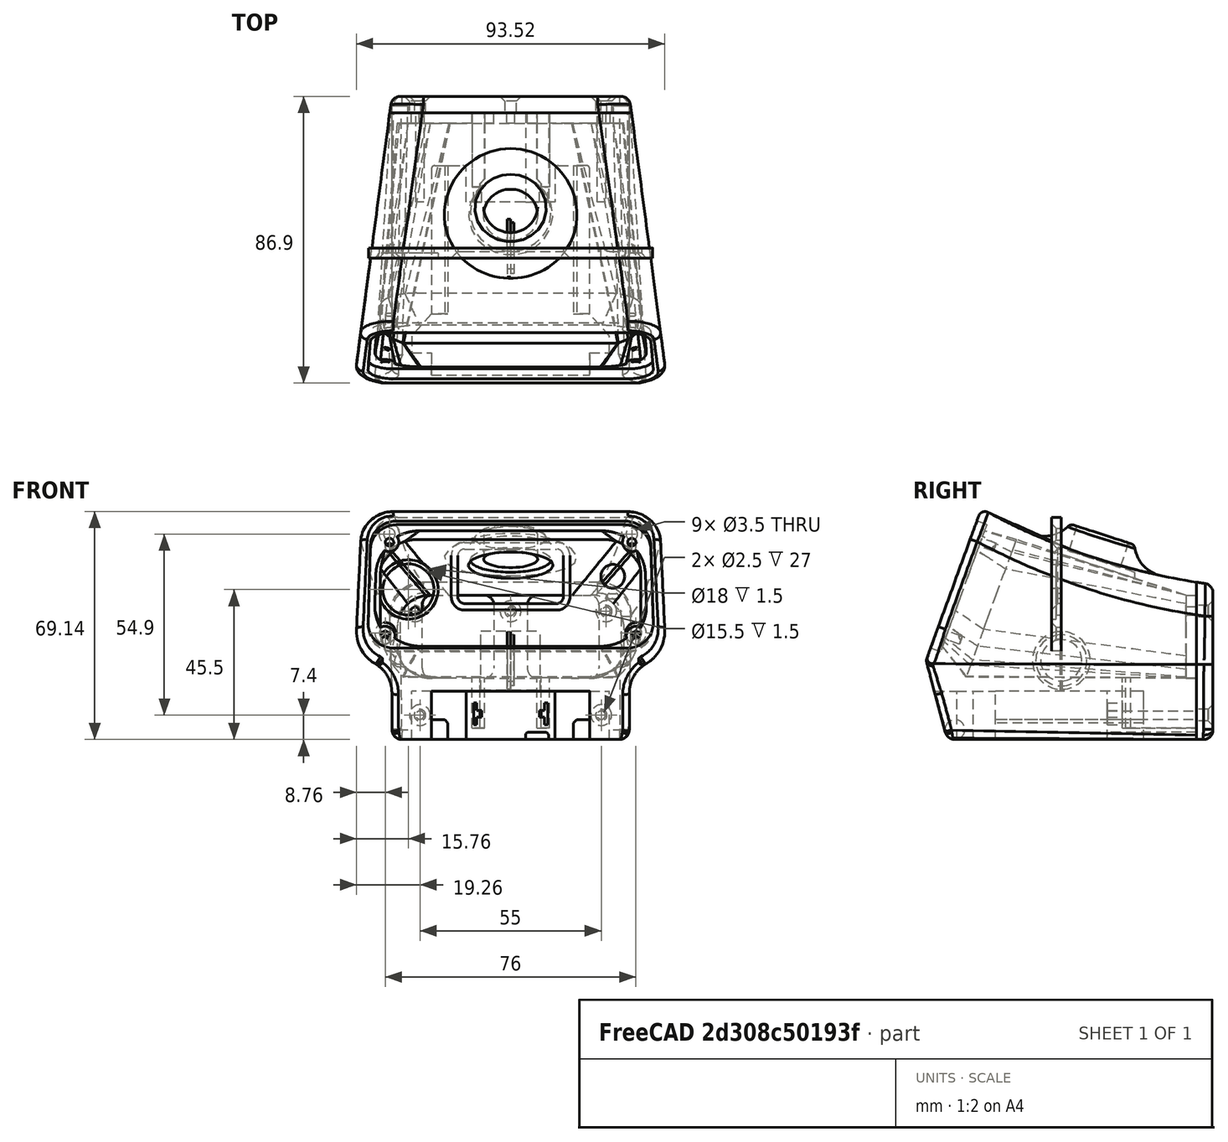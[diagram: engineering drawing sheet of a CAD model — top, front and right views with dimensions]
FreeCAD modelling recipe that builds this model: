
FCSTD DOCUMENT  (FreeCAD 2021.504R24301 +3511 (Git))
Label: solder_station5_snap
License: All rights reserved
LicenseURL: http://en.wikipedia.org/wiki/All_rights_reserved
objects: Sketcher::SketchObject×22, PartDesign::Pocket×11, Part::FeaturePython×6, PartDesign::Fillet×6, App::DocumentObjectGroup×4, PartDesign::Body×4, Mesh::Feature×4, PartDesign::Chamfer×3, PartDesign::FeatureBase×2, PartDesign::Pad×2, PartDesign::Revolution×2, Spreadsheet::Sheet×1, Part::Plane×1, Part::Loft×1, Part::Extrusion×1, Part::MultiCommon×1, Part::Box×1, PartDesign::SubtractiveLoft×1, PartDesign::Groove×1, App::Part×1
note: 119 computed .brp shape members not serialized (recipe doc carries the construction recipe); baked Part::Feature solids carry a one-line shape summary decoded from their .brp

FEATURE [Sketcher::SketchObject] Sketch  label="RearSupport"
  AttachmentOffset = pos=(0,0,-37.8) rot=(0,0,1;0rad)
  FullyConstrained = true
  MapMode = 5
  Placement = pos=(0,37.8,8.4e-15) rot=(1,0,0;1.5708rad)
  Support = -> [XZ_Plane005]
  expr: .AttachmentOffset.Base.z = -<<param>>.mid_depth / 2 + <<param>>.wall
  expr: .Constraints[24] = 3
  expr: .Constraints[37] = <<param>>.bottom_height
  expr: .Constraints[38] = <<param>>.floor
  expr: .Constraints[39] = <<param>>.rear_height - <<param>>.wall
  expr: .Constraints[47] = <<param>>.reart_screw_width2
  expr: .Constraints[48] = <<param>>.rear_screw_width1
  expr: .Constraints[49] = <<param>>.screw_hole
  expr: .Constraints[50] = <<param>>.rear_screw_height
  expr: .Constraints[51] = <<param>>.rear_screw_height
  expr: .Constraints[52] = <<param>>.rear_screw_offset
  sketch-geometry (22):
    g0: LineSegment StartX=-23.8 StartY=19.8 StartZ=0 EndX=-8.1 EndY=19.8 EndZ=0
    g1: LineSegment StartX=26.8 StartY=16.8 StartZ=0 EndX=26.8 EndY=-2.4 EndZ=0
    g2: LineSegment StartX=23.8 StartY=-5.4 StartZ=0 EndX=8.1 EndY=-5.4 EndZ=0
    g3: LineSegment StartX=-26.8 StartY=-2.4 StartZ=0 EndX=-26.8 EndY=16.8 EndZ=0
    g4: LineSegment StartX=-5.1 StartY=16.8 StartZ=0 EndX=-5.1 EndY=-2.4 EndZ=0
    g5: LineSegment StartX=5.1 StartY=16.8 StartZ=0 EndX=5.1 EndY=-2.4 EndZ=0
    g6: LineSegment StartX=8.1 StartY=19.8 StartZ=0 EndX=23.8 EndY=19.8 EndZ=0
    g7: LineSegment StartX=-8.1 StartY=-5.4 StartZ=0 EndX=-23.8 EndY=-5.4 EndZ=0
    g8: ArcOfCircle CenterX=-8.1 CenterY=16.8 CenterZ=0 NormalX=0 NormalY=0 NormalZ=1 AngleXU=0 Radius=3 StartAngle=0 EndAngle=1.5708
    g9: ArcOfCircle CenterX=8.1 CenterY=16.8 CenterZ=0 NormalX=0 NormalY=0 NormalZ=1 AngleXU=0 Radius=3 StartAngle=1.5708 EndAngle=3.14159
    g10: ArcOfCircle CenterX=-8.1 CenterY=-2.4 CenterZ=0 NormalX=0 NormalY=0 NormalZ=1 AngleXU=0 Radius=3 StartAngle=4.71239 EndAngle=6.28319
    g11: ArcOfCircle CenterX=8.1 CenterY=-2.4 CenterZ=0 NormalX=0 NormalY=0 NormalZ=1 AngleXU=0 Radius=3 StartAngle=3.14159 EndAngle=4.71239
    g12: ArcOfCircle CenterX=-23.8 CenterY=16.8 CenterZ=0 NormalX=0 NormalY=0 NormalZ=1 AngleXU=0 Radius=3 StartAngle=1.5708 EndAngle=3.14159
    g13: ArcOfCircle CenterX=-23.8 CenterY=-2.4 CenterZ=0 NormalX=0 NormalY=0 NormalZ=1 AngleXU=0 Radius=3 StartAngle=3.14159 EndAngle=4.71239
    g14: ArcOfCircle CenterX=23.8 CenterY=16.8 CenterZ=0 NormalX=0 NormalY=0 NormalZ=1 AngleXU=0 Radius=3 StartAngle=3e-16 EndAngle=1.5708
    g15: ArcOfCircle CenterX=23.8 CenterY=-2.4 CenterZ=0 NormalX=0 NormalY=0 NormalZ=1 AngleXU=0 Radius=3 StartAngle=4.71239 EndAngle=6.28319
    g16: Circle [constr] CenterX=0 CenterY=-24 CenterZ=0 NormalX=0 NormalY=0 NormalZ=1 AngleXU=0 Radius=3
    g17: Circle CenterX=0 CenterY=14.9 CenterZ=0 NormalX=0 NormalY=0 NormalZ=1 AngleXU=0 Radius=1.25
    g18: Circle CenterX=-29 CenterY=14.9 CenterZ=0 NormalX=0 NormalY=0 NormalZ=1 AngleXU=0 Radius=1.25
    g19: Circle [constr] CenterX=-27.5 CenterY=-16.6 CenterZ=0 NormalX=0 NormalY=0 NormalZ=1 AngleXU=0 Radius=1.25
    g20: Circle [constr] CenterX=27.5 CenterY=-16.6 CenterZ=0 NormalX=0 NormalY=0 NormalZ=1 AngleXU=0 Radius=1.25
    g21: Circle CenterX=29 CenterY=14.9 CenterZ=0 NormalX=0 NormalY=0 NormalZ=1 AngleXU=0 Radius=1.25
  constraints (53):
    c: Horizontal(g0)
    c: Horizontal(g2)
    c: Vertical(g1)
    c: Vertical(g3)
    c: Vertical(g4)
    c: Vertical(g5)
    c: Tangent(g0,g6)
    c: Tangent(g2,g7)
    c: Tangent(g0,g8) = 1.5708
    c: Tangent(g4,g8) = 1.5708
    c: Tangent(g5,g9) = -1.5708
    c: Tangent(g6,g9) = 1.5708
    c: Tangent(g7,g10) = 1.5708
    c: Tangent(g4,g10) = 1.5708
    c: Tangent(g5,g11) = -1.5708
    c: Tangent(g2,g11) = 1.5708
    c: Tangent(g0,g12) = 1.5708
    c: Tangent(g3,g12) = 1.5708
    c: Tangent(g3,g13) = 1.5708
    c: Tangent(g7,g13) = 1.5708
    c: Tangent(g6,g14) = 1.5708
    c: Tangent(g1,g14) = 1.5708
    c: Tangent(g1,g15) = 1.5708
    c: Tangent(g2,g15) = 1.5708
    c: Radius(g9) = 3
    c: Equal(g12,g13)
    c: Equal(g13,g10)
    c: Equal(g10,g8)
    c: Equal(g11,g15)
    c: Equal(g15,g14)
    c: Equal(g14,g9)
    c: DistanceX(g4,g-1) = 5.1
    c: DistanceX(g5,g1) = 21.7
    c: Symmetric(g4,g5,g-2)
    c: Equal(g7,g2)
    c: PointOnObject(g16,g-2)
    c: Radius(g16) = 3
    c: DistanceY(g16,g-1) = 24
    c: DistanceY(g16,g2) = 18.6
    c: DistanceY(g16,g6) = 43.8
    c: PointOnObject(g17,g-2)
    c: Equal(g21,g18)
    c: Equal(g18,g19)
    c: Equal(g19,g20)
    c: Equal(g18,g17)
    c: Symmetric(g20,g19,g-2)
    c: Symmetric(g18,g21,g-2)
    c: DistanceX(g19,g20) = 55
    c: DistanceX(g18,g21) = 58
    c: Diameter(g19) = 2.5
    c: DistanceY(g20,g21) = 31.5
    c: DistanceY(g20,g17) = 31.5
    c: DistanceY(g16,g19) = 7.4
FEATURE [Spreadsheet::Sheet] Spreadsheet  label="param"
  PythonMode = false
  cells = A1=Body; B2=top_depth; C2(top_depth)=70; B3=mid_depth; C3(mid_depth)=82; D3=half is rear reference; B4=bottom_depth; C4(bottom_depth)=75; B6=bottom_width; C6(bottom_width)=72; B7=bottom_height; C7(bottom_height)=24; B8=bottom_angle; C8(bottom_angle)=15; B10=rear_width; C10(rear_width)=72; B11=rear_height; C11(rear_height)=47; F11=41; B13=mid_width; C13(mid_width)=80; B14=mid_height; C14(mid_height)=56; F14=50; B16=front_width1; C16(front_width1)=92; D16=@top; E16=upper; F16=91; B17=front_width2; C17(front_width2)=95; D17=@mid; E17=lower; F17=94; B18=front_height; C18(front_height)=70; F18=64; B19=front_angle; C19(front_angle)=20; B21=wall; C21(wall)=3.2; B22=radius_big; C22(radius_big)=10; B23=radius_small; C23(radius_small)=3; B24=arch; C24(arch)=200; A26=Button; B27=button_offset; C27(button_offset)=10; B28=button_inside_dia; C28(button_inside_dia)=20; B29=button_outside_dia; C29(button_outside_dia)=22; B30=button_height; C30(button_height)=30.6; F30=26; B31=button_extension; C31(button_extension)=8; B32=button_fillet; C32(button_fillet)=12; B33=button_angle; C33(button_angle)=-18; F33=-17; B34=button_hole; C34(button_hole)=16.4; B35=button_hole_center; C35(button_hole_center)=-0.5; A37=Battery Cuts; B38=batt_carveout; C38(batt_carveout)=14.6; B39=batt_rail; C39(batt_rail)=6; B40=batt_rail_length; C40(batt_rail_length)=45; A42=Terminals; B43=terminal_height; C43(terminal_height)=6.6; B44=terminal_thickness; C44(terminal_thickness)=1; B45=terminal_seperation; C45(terminal_seperation)=21.5; B46=terminal_offset; C46(terminal_offset)=4.5; B47=terminal_depth; C47(terminal_depth)=22.5; A49=Box Interior; B50=floor; C50(floor)=18.6; B51=rear_inside_width; C51(rear_inside_width)==C10 - C21; D51=calc; B52=rear_inside_height; C52(rear_inside_height)==C11 - C21; D52=calc; B53=mid_inside_width; C53(mid_inside_width)==C13; D53=calc; B54=mid_inside_height; C54(mid_inside_height)==C14 + 7; D54=calc; F54=6; B55=front_inside_width1; C55(front_inside_width1)==C62 - C58 * 2; D55=calc; E55=upper; B56=front_inside_width2; C56(front_inside_width2)==C63 - C58 * 2; D56=calc; E56=lower; B57=front_inside_height; C57(front_inside_height)==C64 - C59 * 2; D57=calc; B58=front_width_lip_width; C58(front_width_lip_width)=3; B59=front_inside_lip_height; C59(front_inside_lip_height)=2; A61=Face; B62=face_width1; C62(face_width1)==84 + 1; B63=face_width2; C63(face_width2)==85.5 + 1; B64=face_height; C64(face_height)=41; F64=35; B65=face_thickness; C65(face_thickness)=3; B66=face_radius; C66(face_radius)=8; B67=face_offset; C67(face_offset)=2.8; F67=2.8; A69=Screws; B70=screw_hole; C70(screw_hole)=2.5; B72=front_screw_width1; C72(front_screw_width1)=73.5; D72=upper; B73=front_screw_width2; C73(front_screw_width2)=76; D73=lower; B74=front_screw_height; C74(front_screw_height)=30; F74=24; B75=front_screw_offset; C75(front_screw_offset)=5.5; B77=rear_screw_width1; C77(rear_screw_width1)=58; B78=reart_screw_width2; C78(reart_screw_width2)=55; B79=rear_screw_height; C79(rear_screw_height)=31.5; F79=25.5; B80=rear_screw_offset; C80(rear_screw_offset)=7.4; A82=Back; B83=back_thickness; C83(back_thickness)=5
FEATURE [Sketcher::SketchObject] Sketch008  label="SketchButtonHole"
  AttachmentOffset = pos=(0,-0.5,30.6) rot=(1,0,0;-0.314159rad)
  FullyConstrained = true
  MapMode = 5
  Placement = pos=(0,-0.5,30.6) rot=(1,0,0;5.96903rad)
  Support = -> [XY_Plane005]
  expr: .AttachmentOffset.Base.y = <<param>>.button_hole_center
  expr: .AttachmentOffset.Base.z = <<param>>.button_height
  expr: .AttachmentOffset.Rotation.Angle = <<param>>.button_angle
  expr: .Constraints[0] = <<param>>.button_hole
  expr: .Constraints[2] = <<param>>.button_offset
  sketch-geometry (1):
    g0: Circle CenterX=0 CenterY=10 CenterZ=0 NormalX=0 NormalY=0 NormalZ=1 AngleXU=0 Radius=8.2
  constraints (3):
    c: Diameter(g0) = 16.4
    c: PointOnObject(g0,g-2)
    c: DistanceY(g-1,g0) = 10
FEATURE [Sketcher::SketchObject] Sketch012  label="SketchSide"
  AttachmentOffset = pos=(2.5,0,0) rot=(0,0,1;0rad)
  FullyConstrained = true
  MapMode = 5
  Placement = pos=(6e-16,2.5,-6e-16) rot=(0.57735,0.57735,0.57735;2.0944rad)
  Support = -> [YZ_Plane006]
  expr: .AttachmentOffset.Base.x = <<param>>.back_thickness / 2
  expr: .Constraints[14] = <<param>>.bottom_height
  expr: .Constraints[15] = <<param>>.radius_small
  expr: .Constraints[16] = 90 - <<param>>.bottom_angle
  expr: .Constraints[17] = 90 - <<param>>.front_angle
  expr: .Constraints[21] = <<param>>.front_height
  expr: .Constraints[4] = <<param>>.rear_height - <<param>>.bottom_height
  expr: .Constraints[5] = <<param>>.arch
  expr: .Constraints[6] = <<param>>.mid_depth + <<param>>.back_thickness
  sketch-geometry (7):
    g0: LineSegment StartX=43.5 StartY=0 StartZ=0 EndX=43.5 EndY=23 EndZ=0
    g1: LineSegment StartX=-43.5 StartY=0 StartZ=0 EndX=-26.7574 EndY=46 EndZ=0
    g2: ArcOfCircle CenterX=69.5235 CenterY=221.3 CenterZ=0 NormalX=0 NormalY=0 NormalZ=1 AngleXU=0 Radius=200 StartAngle=4.21013 EndAngle=4.5819
    g3: LineSegment StartX=-43.5 StartY=0 StartZ=0 EndX=-37.665 EndY=-21.7765 EndZ=0
    g4: LineSegment StartX=-34.7673 StartY=-24 StartZ=0 EndX=43.5 EndY=-24 EndZ=0
    g5: LineSegment StartX=43.5 StartY=-24 StartZ=0 EndX=43.5 EndY=0 EndZ=0
    g6: ArcOfCircle CenterX=-34.7672 CenterY=-21 CenterZ=0 NormalX=0 NormalY=0 NormalZ=1 AngleXU=0 Radius=3 StartAngle=3.4034 EndAngle=4.71238
  constraints (22):
    c: PointOnObject(g1,g-1)
    c: Vertical(g0)
    c: Coincident(g2,g0)
    c: Symmetric(g1,g0,g-2)
    c: DistanceY(g0,g0) = 23
    c: Radius(g2) = 200
    c: DistanceX(g1,g0) = 87
    c: Horizontal(g4)
    c: Coincident(g5,g4)
    c: Vertical(g5)
    c: Coincident(g6,g3)
    c: Coincident(g6,g4)
    c: Tangent(g6,g4)
    c: Tangent(g6,g3)
    c: DistanceY(g4,g-1) = 24
    c: Radius(g6) = 3
    c: Angle(g3,g-1) = 1.309
    c: Angle(g-1,g1) = 1.22173
    c: Coincident(g3,g1)
    c: Coincident(g5,g0)
    c: Coincident(g2,g1)
    c: DistanceY(g4,g1) = 70
FEATURE [Sketcher::SketchObject] Sketch018  label="SketchBat1"
  AttachmentOffset = pos=(0,0,-24) rot=(0,0,1;0rad)
  FullyConstrained = true
  MapMode = 5
  Placement = pos=(0,0,-24) rot=(0,0,1;0rad)
  Support = -> [XY_Plane005]
  expr: .AttachmentOffset.Base.z = -<<param>>.bottom_height
  expr: .Constraints[63] = <<param>>.batt_rail_length
  expr: .Constraints[64] = <<param>>.mid_depth / 2
  sketch-geometry (21):
    g0: LineSegment StartX=-24 StartY=-41.7082 StartZ=0 EndX=24 EndY=-41.7082 EndZ=0
    g1: LineSegment StartX=24 StartY=-41.7082 StartZ=0 EndX=24 EndY=-31.7082 EndZ=0
    g2: LineSegment StartX=24 StartY=-31.7082 StartZ=0 EndX=30 EndY=-31.7082 EndZ=0
    g3: LineSegment StartX=30 StartY=-31.7082 StartZ=0 EndX=30 EndY=-26.7082 EndZ=0
    g4: LineSegment StartX=30 StartY=-26.7082 StartZ=0 EndX=24 EndY=-20 EndZ=0
    g5: LineSegment StartX=24 StartY=-20 StartZ=0 EndX=24 EndY=24 EndZ=0
    g6: LineSegment StartX=13.5 StartY=24 StartZ=0 EndX=13.5 EndY=14 EndZ=0
    g7: LineSegment StartX=13.5 StartY=14 StartZ=0 EndX=-13.5 EndY=14 EndZ=0
    g8: LineSegment StartX=-13.5 StartY=14 StartZ=0 EndX=-13.5 EndY=24 EndZ=0
    g9: LineSegment StartX=-24 StartY=24 StartZ=0 EndX=-24 EndY=-20 EndZ=0
    g10: LineSegment StartX=-24 StartY=-20 StartZ=0 EndX=-30 EndY=-26.7082 EndZ=0
    g11: LineSegment StartX=-30 StartY=-26.7082 StartZ=0 EndX=-30 EndY=-31.7082 EndZ=0
    g12: LineSegment StartX=-30 StartY=-31.7082 StartZ=0 EndX=-24 EndY=-31.7082 EndZ=0
    g13: LineSegment StartX=-24 StartY=-31.7082 StartZ=0 EndX=-24 EndY=-41.7082 EndZ=0
    g14: Circle [constr] CenterX=0 CenterY=41 CenterZ=0 NormalX=0 NormalY=0 NormalZ=1 AngleXU=0 Radius=4
    g15: ArcOfCircle CenterX=-14.5 CenterY=24 CenterZ=0 NormalX=0 NormalY=0 NormalZ=1 AngleXU=0 Radius=1 StartAngle=6.28318 EndAngle=7.85399
    g16: LineSegment StartX=-23 StartY=25 StartZ=0 EndX=-14.5 EndY=25 EndZ=0
    g17: LineSegment StartX=14.5 StartY=25 StartZ=0 EndX=23 EndY=25 EndZ=0
    g18: ArcOfCircle CenterX=-23 CenterY=24 CenterZ=0 NormalX=0 NormalY=0 NormalZ=1 AngleXU=0 Radius=1 StartAngle=1.57079 EndAngle=3.1416
    g19: ArcOfCircle CenterX=14.5 CenterY=24 CenterZ=0 NormalX=0 NormalY=0 NormalZ=1 AngleXU=0 Radius=1 StartAngle=1.5708 EndAngle=3.14159
    g20: ArcOfCircle CenterX=23 CenterY=24 CenterZ=0 NormalX=0 NormalY=0 NormalZ=1 AngleXU=0 Radius=1.00001 StartAngle=2.75124e-06 EndAngle=1.5708
  constraints (65):
    c: Horizontal(g0)
    c: Coincident(g1,g0)
    c: Vertical(g1)
    c: Coincident(g2,g1)
    c: Horizontal(g2)
    c: Coincident(g3,g2)
    c: Coincident(g3,g4)
    c: Vertical(g5)
    c: Coincident(g6,g7)
    c: Coincident(g7,g8)
    c: Vertical(g8)
    c: Vertical(g9)
    c: Coincident(g10,g11)
    c: Vertical(g11)
    c: Coincident(g11,g12)
    c: Horizontal(g12)
    c: Coincident(g12,g13)
    c: Equal(g6,g8)
    c: Equal(g5,g9)
    c: Equal(g4,g10)
    c: Equal(g3,g11)
    c: Equal(g12,g2)
    c: Equal(g1,g13)
    c: Coincident(g13,g0)
    c: Vertical(g13)
    c: DistanceX(g7,g7) = 27
    c: Symmetric(g7,g6,g-2)
    c: Distance(g4) = 9
    c: Vertical(g3)
    c: DistanceY(g3,g3) = 5
    c: DistanceX(g2,g2) = 6
    c: DistanceY(g1,g1) = 10
    c: DistanceX(g0,g0) = 48
    c: PointOnObject(g14,g-2)
    c: Coincident(g9,g10)
    c: Coincident(g5,g4)
    c: Coincident(g15,g8)
    c: Coincident(g16,g15)
    c: Tangent(g15,g8)
    c: Horizontal(g16)
    c: Horizontal(g17)
    c: DistanceX(g9,g5) = 48
    c: Symmetric(g4,g9,g-2)
    c: Equal(g16,g17)
    c: Coincident(g18,g9)
    c: Coincident(g18,g16)
    c: Equal(g18,g15)
    c: Tangent(g18,g16)
    c: Tangent(g18,g9)
    c: DistanceY(g6,g17) = 11
    c: Vertical(g6)
    c: Coincident(g19,g6)
    c: Coincident(g19,g17)
    c: Coincident(g20,g17)
    c: Coincident(g20,g5)
    c: Tangent(g20,g17)
    c: Tangent(g20,g5)
    c: Tangent(g19,g6)
    c: Tangent(g19,g17)
    c: Equal(g15,g19)
    c: Radius(g19) = 1
    c: Radius(g14) = 4
    c: DistanceY(g15,g14) = 16
    c: DistanceY(g9,g16) = 45
    c: DistanceY(g-1,g14) = 41
FEATURE [Sketcher::SketchObject] Sketch019  label="SketchBat2"
  AttachmentOffset = pos=(0,0,-25) rot=(0,0,1;0rad)
  FullyConstrained = true
  MapMode = 5
  Placement = pos=(0,25,5.6e-15) rot=(1,0,0;1.5708rad)
  Support = -> [XZ_Plane005]
  expr: .AttachmentOffset.Base.z = -<<param>>.mid_depth / 2 + 16
  expr: .Constraints[17] = <<param>>.bottom_height
  expr: .Constraints[18] = <<param>>.batt_rail
  expr: .Constraints[19] = 48.01mm
  sketch-geometry (10):
    g0: LineSegment StartX=-24.005 StartY=-18 StartZ=0 EndX=-20.005 EndY=-18 EndZ=0
    g1: LineSegment StartX=-19.005 StartY=-24 StartZ=0 EndX=-24.005 EndY=-24 EndZ=0
    g2: LineSegment StartX=-24.005 StartY=-24 StartZ=0 EndX=-24.005 EndY=-18 EndZ=0
    g3: LineSegment StartX=24.005 StartY=-18 StartZ=0 EndX=20.005 EndY=-18 EndZ=0
    g4: LineSegment StartX=19.005 StartY=-24 StartZ=0 EndX=24.005 EndY=-24 EndZ=0
    g5: LineSegment StartX=24.005 StartY=-24 StartZ=0 EndX=24.005 EndY=-18 EndZ=0
    g6: LineSegment StartX=-19.005 StartY=-19 StartZ=0 EndX=-19.005 EndY=-24 EndZ=0
    g7: LineSegment StartX=19.005 StartY=-24 StartZ=0 EndX=19.005 EndY=-19 EndZ=0
    g8: LineSegment StartX=-20.005 StartY=-18 StartZ=0 EndX=-19.005 EndY=-19 EndZ=0
    g9: LineSegment StartX=19.005 StartY=-19 StartZ=0 EndX=20.005 EndY=-18 EndZ=0
  constraints (29):
    c: Coincident(g1,g2)
    c: Coincident(g2,g0)
    c: Horizontal(g0)
    c: Horizontal(g1)
    c: Vertical(g2)
    c: Coincident(g4,g5)
    c: Coincident(g5,g3)
    c: Horizontal(g3)
    c: Horizontal(g4)
    c: Vertical(g5)
    c: Coincident(g6,g1)
    c: Vertical(g6)
    c: Equal(g1,g4)
    c: Coincident(g7,g4)
    c: Vertical(g7)
    c: Equal(g6,g7)
    c: Symmetric(g1,g4,g-2)
    c: DistanceY(g1,g-1) = 24
    c: DistanceY(g4,g3) = 6
    c: DistanceX(g1,g4) = 48.01
    c: DistanceX(g4,g4) = 5
    c: Coincident(g8,g0)
    c: Coincident(g8,g6)
    c: Coincident(g9,g7)
    c: Coincident(g9,g3)
    c: Equal(g0,g3)
    c: Equal(g2,g5)
    c: DistanceX(g0,g0) = 4
    c: DistanceY(g1,g6) = 5
FEATURE [Sketcher::SketchObject] Sketch021  label="SketchButton"
  AttachmentOffset = pos=(10,30.6,0) rot=(0,0,1;-0.314159rad)
  FullyConstrained = true
  MapMode = 5
  Placement = pos=(-4.6e-15,10,30.6) rot=(-0.506732,-0.697457,-0.506732;4.35963rad)
  Support = -> [YZ_Plane005]
  expr: .AttachmentOffset.Base.x = <<param>>.button_offset
  expr: .AttachmentOffset.Base.y = <<param>>.button_height
  expr: .AttachmentOffset.Rotation.Angle = <<param>>.button_angle
  expr: .Constraints[6] = <<param>>.button_extension
  expr: .Constraints[7] = <<param>>.button_outside_dia / 2
  sketch-geometry (5):
    g0: LineSegment StartX=0 StartY=0 StartZ=0 EndX=0 EndY=8 EndZ=0
    g1: LineSegment StartX=0 StartY=8 StartZ=0 EndX=9 EndY=8 EndZ=0
    g2: LineSegment StartX=0 StartY=0 StartZ=0 EndX=11 EndY=0 EndZ=0
    g3: LineSegment StartX=11 StartY=0 StartZ=0 EndX=11 EndY=6 EndZ=0
    g4: ArcOfCircle CenterX=9 CenterY=6 CenterZ=0 NormalX=0 NormalY=0 NormalZ=1 AngleXU=0 Radius=2 StartAngle=1e-16 EndAngle=1.5708
  constraints (13):
    c: Coincident(g0,g-1)
    c: PointOnObject(g0,g-2)
    c: Coincident(g1,g0)
    c: Horizontal(g1)
    c: Coincident(g2,g0)
    c: Horizontal(g2)
    c: DistanceY(g0,g0) = 8
    c: DistanceX(g2,g2) = 11
    c: Coincident(g3,g2)
    c: Vertical(g3)
    c: Radius(g4) = 2
    c: Tangent(g4,g1) = 1.5708
    c: Tangent(g4,g3) = -1.5708
FEATURE [Sketcher::SketchObject] Sketch022  label="SketchRearInside"
  AttachmentOffset = pos=(0,0,-37.8) rot=(0,0,1;0rad)
  FullyConstrained = true
  MapMode = 5
  Placement = pos=(0,37.8,8.4e-15) rot=(1,0,0;1.5708rad)
  Support = -> [XZ_Plane005]
  expr: .AttachmentOffset.Base.z = -<<param>>.mid_depth / 2 + <<param>>.wall
  expr: .Constraints[12] = <<param>>.radius_big
  expr: .Constraints[18] = <<param>>.rear_inside_width
  expr: .Constraints[26] = <<param>>.bottom_height
  expr: .Constraints[27] = <<param>>.rear_inside_height
  expr: .Constraints[29] = <<param>>.floor
  sketch-geometry (9):
    g0: LineSegment StartX=-34.4 StartY=9.80003 StartZ=0 EndX=-34.4 EndY=4.59997 EndZ=0
    g1: LineSegment StartX=-24.4 StartY=-5.4 StartZ=0 EndX=24.4 EndY=-5.4 EndZ=0
    g2: LineSegment StartX=34.4 StartY=4.59997 StartZ=0 EndX=34.4 EndY=9.80003 EndZ=0
    g3: LineSegment StartX=-24.4 StartY=19.8 StartZ=0 EndX=24.4 EndY=19.8 EndZ=0
    g4: ArcOfCircle CenterX=24.4 CenterY=9.8 CenterZ=0 NormalX=0 NormalY=0 NormalZ=1 AngleXU=0 Radius=10 StartAngle=3.49027e-06 EndAngle=1.57079
    g5: ArcOfCircle CenterX=24.4 CenterY=4.6 CenterZ=0 NormalX=0 NormalY=0 NormalZ=1 AngleXU=0 Radius=10 StartAngle=4.71239 EndAngle=6.28318
    g6: ArcOfCircle CenterX=-24.4 CenterY=9.8 CenterZ=0 NormalX=0 NormalY=0 NormalZ=1 AngleXU=0 Radius=10 StartAngle=1.5708 EndAngle=3.14159
    g7: ArcOfCircle CenterX=-24.4 CenterY=4.6 CenterZ=0 NormalX=0 NormalY=0 NormalZ=1 AngleXU=0 Radius=10 StartAngle=3.1416 EndAngle=4.71239
    g8: Circle [constr] CenterX=0 CenterY=-24 CenterZ=0 NormalX=0 NormalY=0 NormalZ=1 AngleXU=0 Radius=3
  constraints (30):
    c: Vertical(g0)
    c: Horizontal(g1)
    c: Vertical(g2)
    c: Horizontal(g3)
    c: Equal(g3,g1)
    c: Equal(g0,g2)
    c: Coincident(g4,g3)
    c: Coincident(g4,g2)
    c: Coincident(g5,g2)
    c: Coincident(g5,g1)
    c: Coincident(g6,g0)
    c: Coincident(g6,g3)
    c: Radius(g6) = 10
    c: Equal(g6,g4)
    c: Equal(g4,g5)
    c: Coincident(g7,g1)
    c: Coincident(g7,g0)
    c: Equal(g5,g7)
    c: DistanceX(g0,g2) = 68.8
    c: Symmetric(g0,g2,g-2)
    c: Tangent(g4,g2)
    c: Tangent(g4,g3)
    c: Tangent(g5,g2)
    c: Tangent(g5,g1)
    c: Tangent(g6,g3)
    c: PointOnObject(g8,g-2)
    c: DistanceY(g8,g-1) = 24
    c: DistanceY(g8,g3) = 43.8
    c: Radius(g8) = 3
    c: DistanceY(g8,g1) = 18.6
FEATURE [Sketcher::SketchObject] Sketch024  label="SketchFaceCut"
  AttachmentOffset = pos=(0,0,37.6) rot=(1,0,0;-0.349066rad)
  FullyConstrained = true
  MapMode = 5
  Placement = pos=(0,-37.6,-8.3e-15) rot=(-1,0,0;5.06145rad)
  Support = -> [XZ_Plane005]
  expr: .AttachmentOffset.Base.z = <<param>>.mid_depth / 2 - <<param>>.face_thickness - 0.4
  expr: .AttachmentOffset.Rotation.Angle = -<<param>>.front_angle
  expr: .Constraints[13] = <<param>>.face_radius
  expr: .Constraints[22] = <<param>>.face_width1
  expr: .Constraints[23] = <<param>>.face_width2
  expr: .Constraints[24] = <<param>>.face_offset
  expr: .Constraints[25] = <<param>>.face_height
  sketch-geometry (8):
    g0: LineSegment StartX=-34.5035 StartY=43.8 StartZ=0 EndX=34.5037 EndY=43.8 EndZ=0
    g1: LineSegment StartX=42.5001 StartY=36.0399 StartZ=0 EndX=43.25 EndY=11.0399 EndZ=0
    g2: LineSegment StartX=35.2536 StartY=2.8 StartZ=0 EndX=-35.2536 EndY=2.8 EndZ=0
    g3: LineSegment StartX=-43.25 StartY=11.0399 StartZ=0 EndX=-42.4999 EndY=36.0399 EndZ=0
    g4: ArcOfCircle CenterX=34.5037 CenterY=35.8 CenterZ=0 NormalX=0 NormalY=0 NormalZ=1 AngleXU=0 Radius=8 StartAngle=0.0299879 EndAngle=1.5708
    g5: ArcOfCircle CenterX=35.2536 CenterY=10.8 CenterZ=0 NormalX=0 NormalY=0 NormalZ=1 AngleXU=0 Radius=8 StartAngle=4.71239 EndAngle=6.31317
    g6: ArcOfCircle CenterX=-34.5035 CenterY=35.8 CenterZ=0 NormalX=0 NormalY=0 NormalZ=1 AngleXU=0 Radius=8 StartAngle=1.5708 EndAngle=3.1116
    g7: ArcOfCircle CenterX=-35.2536 CenterY=10.8 CenterZ=0 NormalX=0 NormalY=0 NormalZ=1 AngleXU=0 Radius=8 StartAngle=3.1116 EndAngle=4.71239
  constraints (27):
    c: Horizontal(g0)
    c: Coincident(g4,g0)
    c: Coincident(g4,g1)
    c: Coincident(g5,g1)
    c: Coincident(g5,g2)
    c: Coincident(g6,g0)
    c: Coincident(g6,g3)
    c: Coincident(g7,g3)
    c: Coincident(g7,g2)
    c: Equal(g1,g3)
    c: Equal(g4,g6)
    c: Equal(g6,g7)
    c: Equal(g7,g5)
    c: Radius(g4) = 8
    c: Tangent(g6,g3)
    c: Tangent(g7,g3)
    c: Tangent(g7,g2)
    c: Tangent(g6,g0)
    c: Tangent(g4,g0)
    c: Tangent(g4,g1)
    c: Tangent(g5,g1)
    c: Tangent(g5,g2)
    c: DistanceX(g3,g1) = 85
    c: DistanceX(g3,g1) = 86.5
    c: DistanceY(g-1,g2) = 2.8
    c: DistanceY(g2,g0) = 41
    c: Symmetric(g2,g2,g-2)
FEATURE [Sketcher::SketchObject] Sketch025  label="SketchMidInside"
  AttachmentOffset = pos=(0,0,27) rot=(1,0,0;-0.349066rad)
  FullyConstrained = true
  MapMode = 5
  Placement = pos=(0,-27,-6e-15) rot=(-1,0,0;5.06145rad)
  Support = -> [XZ_Plane005]
  expr: .AttachmentOffset.Base.z = <<param>>.mid_depth / 2 - 14
  expr: .AttachmentOffset.Rotation.Angle = -<<param>>.front_angle
  expr: .Constraints[10] = <<param>>.radius_big + 1
  expr: .Constraints[11] = <<param>>.floor
  expr: .Constraints[12] = Spreadsheet.mid_inside_width - 1
  expr: .Constraints[14] = <<param>>.mid_inside_height
  expr: .Constraints[23] = <<param>>.mid_width - 15
  expr: .Constraints[4] = <<param>>.bottom_height
  sketch-geometry (9):
    g0: LineSegment StartX=-28.5 StartY=39 StartZ=0 EndX=28.5 EndY=39 EndZ=0
    g1: LineSegment StartX=39.5 StartY=28 StartZ=0 EndX=39.5 EndY=10 EndZ=0
    g2: LineSegment StartX=32.5 StartY=-5.4 StartZ=0 EndX=-32.5 EndY=-5.4 EndZ=0
    g3: LineSegment StartX=-39.5 StartY=10 StartZ=0 EndX=-39.5 EndY=28 EndZ=0
    g4: Circle [constr] CenterX=0 CenterY=-24 CenterZ=0 NormalX=0 NormalY=0 NormalZ=1 AngleXU=0 Radius=3
    g5: ArcOfCircle CenterX=-28.5 CenterY=28 CenterZ=0 NormalX=0 NormalY=0 NormalZ=1 AngleXU=0 Radius=11 StartAngle=1.5708 EndAngle=3.14159
    g6: ArcOfCircle CenterX=28.5 CenterY=28 CenterZ=0 NormalX=0 NormalY=0 NormalZ=1 AngleXU=0 Radius=11 StartAngle=0 EndAngle=1.5708
    g7: ArcOfCircle CenterX=-15.553 CenterY=11.5941 CenterZ=0 NormalX=0 NormalY=0 NormalZ=1 AngleXU=0 Radius=24 StartAngle=3.20806 EndAngle=3.92838
    g8: ArcOfCircle CenterX=15.553 CenterY=11.5941 CenterZ=0 NormalX=0 NormalY=0 NormalZ=1 AngleXU=0 Radius=24 StartAngle=5.4964 EndAngle=6.21672
  constraints (25):
    c: Vertical(g1)
    c: Vertical(g3)
    c: PointOnObject(g4,g-2)
    c: Radius(g4) = 3
    c: DistanceY(g4,g-1) = 24
    c: Tangent(g3,g5) = 1.5708
    c: Tangent(g0,g5) = 1.5708
    c: Tangent(g0,g6) = 1.5708
    c: Tangent(g1,g6) = 1.5708
    c: Equal(g6,g5)
    c: Radius(g6) = 11
    c: DistanceY(g4,g2) = 18.6
    c: DistanceX(g3,g1) = 79
    c: Symmetric(g2,g2,g-2)
    c: DistanceY(g4,g0) = 63
    c: Symmetric(g0,g0,g-2)
    c: Equal(g3,g1)
    c: Coincident(g7,g2)
    c: Coincident(g8,g1)
    c: Coincident(g8,g2)
    c: Coincident(g7,g3)
    c: Equal(g8,g7)
    c: Radius(g8) = 24
    c: DistanceX(g2,g2) = 65
    c: DistanceY(g1,g1) = 18
FEATURE [Sketcher::SketchObject] Sketch026  label="SketchFrontScrews"
  AttachmentOffset = pos=(0,0,38) rot=(1,0,0;-0.349066rad)
  FullyConstrained = true
  MapMode = 5
  Placement = pos=(0,-38,-8.4e-15) rot=(-1,0,0;5.06145rad)
  Support = -> [XZ_Plane005]
  expr: .AttachmentOffset.Base.z = <<param>>.mid_depth / 2 - <<param>>.face_thickness
  expr: .AttachmentOffset.Rotation.Angle = -<<param>>.front_angle
  expr: .Constraints[0] = <<param>>.front_screw_width1
  expr: .Constraints[13] = <<param>>.screw_hole
  expr: .Constraints[1] = <<param>>.front_screw_width2
  expr: .Constraints[2] = <<param>>.front_screw_height
  expr: .Constraints[9] = <<param>>.face_offset + <<param>>.front_screw_offset
  sketch-geometry (6):
    g0: Circle CenterX=-36.75 CenterY=38.3 CenterZ=0 NormalX=0 NormalY=0 NormalZ=1 AngleXU=0 Radius=1.25
    g1: Circle CenterX=36.75 CenterY=38.3 CenterZ=0 NormalX=0 NormalY=0 NormalZ=1 AngleXU=0 Radius=1.25
    g2: Circle CenterX=-38 CenterY=8.3 CenterZ=0 NormalX=0 NormalY=0 NormalZ=1 AngleXU=0 Radius=1.25
    g3: Circle CenterX=38 CenterY=8.3 CenterZ=0 NormalX=0 NormalY=0 NormalZ=1 AngleXU=0 Radius=1.25
    g4: LineSegment [constr] StartX=-36.75 StartY=38.3 StartZ=0 EndX=36.75 EndY=38.3 EndZ=0
    g5: LineSegment [constr] StartX=-38 StartY=8.3 StartZ=0 EndX=38 EndY=8.3 EndZ=0
  constraints (14):
    c: DistanceX(g0,g1) = 73.5
    c: DistanceX(g2,g3) = 76
    c: DistanceY(g3,g1) = 30
    c: Coincident(g4,g0)
    c: Coincident(g4,g1)
    c: Coincident(g5,g2)
    c: Coincident(g5,g3)
    c: Symmetric(g2,g3,g-2)
    c: Symmetric(g0,g1,g-2)
    c: DistanceY(g-1,g3) = 8.3
    c: Equal(g0,g2)
    c: Equal(g2,g3)
    c: Equal(g3,g1)
    c: Diameter(g0) = 2.5
FEATURE [Sketcher::SketchObject] Sketch023  label="SketchFrontInside"
  AttachmentOffset = pos=(0,0,38) rot=(1,0,0;-0.349066rad)
  ExternalGeometry = -> [Sketch026,Sketch024]
  FullyConstrained = true
  MapMode = 5
  Placement = pos=(0,-38,-8.4e-15) rot=(-1,0,0;5.06145rad)
  Support = -> [XZ_Plane005]
  expr: .AttachmentOffset.Base.z = <<param>>.mid_depth / 2 - <<param>>.face_thickness
  expr: .AttachmentOffset.Rotation.Angle = -<<param>>.front_angle
  sketch-geometry (16):
    g0: LineSegment StartX=-27.5 StartY=4.93681 StartZ=0 EndX=27.5 EndY=4.93681 EndZ=0
    g1: LineSegment StartX=27.5 StartY=41.9368 StartZ=0 EndX=-27.5 EndY=41.9368 EndZ=0
    g2: LineSegment StartX=-40.95 StartY=28.0001 StartZ=0 EndX=-41.25 EndY=18.0001 EndZ=0
    g3: LineSegment StartX=40.95 StartY=28 StartZ=0 EndX=41.25 EndY=18 EndZ=0
    g4: ArcOfCircle CenterX=36.75 CenterY=38.3 CenterZ=0 NormalX=0 NormalY=0 NormalZ=1 AngleXU=0 Radius=3 StartAngle=2.46996 EndAngle=5.23357
    g5: ArcOfCircle CenterX=27.5 CenterY=27.5965 CenterZ=0 NormalX=0 NormalY=0 NormalZ=1 AngleXU=0 Radius=13.4561 StartAngle=0.0299886 EndAngle=0.646116
    g6: ArcOfCircle CenterX=27.5 CenterY=27.5965 CenterZ=0 NormalX=0 NormalY=0 NormalZ=1 AngleXU=0 Radius=14.3403 StartAngle=1.06869 EndAngle=1.5708
    g7: ArcOfCircle CenterX=38 CenterY=8.3 CenterZ=0 NormalX=0 NormalY=0 NormalZ=1 AngleXU=0 Radius=3 StartAngle=1.04133 EndAngle=3.41706
    g8: ArcOfCircle CenterX=27.5 CenterY=17.5875 CenterZ=0 NormalX=0 NormalY=0 NormalZ=1 AngleXU=0 Radius=13.7562 StartAngle=5.77461 EndAngle=6.31317
    g9: ArcOfCircle CenterX=27.5 CenterY=17.5875 CenterZ=0 NormalX=0 NormalY=0 NormalZ=1 AngleXU=0 Radius=12.6507 StartAngle=4.71239 EndAngle=5.35813
    g10: ArcOfCircle CenterX=-36.75 CenterY=38.3 CenterZ=0 NormalX=0 NormalY=0 NormalZ=1 AngleXU=0 Radius=3 StartAngle=4.19123 EndAngle=6.95482
    g11: ArcOfCircle CenterX=-27.5 CenterY=27.5965 CenterZ=0 NormalX=0 NormalY=0 NormalZ=1 AngleXU=0 Radius=13.456 StartAngle=2.49548 EndAngle=3.1116
    g12: ArcOfCircle CenterX=-27.5 CenterY=27.5965 CenterZ=0 NormalX=0 NormalY=0 NormalZ=1 AngleXU=0 Radius=14.3403 StartAngle=1.5708 EndAngle=2.0729
    g13: ArcOfCircle CenterX=-38 CenterY=8.3 CenterZ=0 NormalX=0 NormalY=0 NormalZ=1 AngleXU=0 Radius=3 StartAngle=6.00771 EndAngle=8.38345
    g14: ArcOfCircle CenterX=-27.5 CenterY=17.5875 CenterZ=0 NormalX=0 NormalY=0 NormalZ=1 AngleXU=0 Radius=13.7562 StartAngle=3.1116 EndAngle=3.65016
    g15: ArcOfCircle CenterX=-27.5 CenterY=17.5875 CenterZ=0 NormalX=0 NormalY=0 NormalZ=1 AngleXU=0 Radius=12.6507 StartAngle=4.06665 EndAngle=4.71239
  constraints (42):
    c: Symmetric(g0,g0,g-2)
    c: Symmetric(g1,g1,g-2)
    c: DistanceY(g3,g3) = 10
    c: Equal(g3,g2)
    c: Equal(g1,g0)
    c: DistanceX(g1,g1) = 55
    c: Coincident(g4,g-3)
    c: Coincident(g5,g4)
    c: Coincident(g6,g4)
    c: Radius(g4) = 3
    c: Tangent(g5,g3) = 1.5708
    c: Parallel(g3,g-8)
    c: Tangent(g6,g1) = -1.5708
    c: DistanceX(g3,g-8) = 2
    c: Parallel(g-7,g2)
    c: DistanceX(g-7,g2) = 2
    c: Coincident(g7,g-4)
    c: Coincident(g8,g7)
    c: Coincident(g9,g7)
    c: Tangent(g8,g3) = 1.5708
    c: Tangent(g9,g0) = -1.5708
    c: Coincident(g9,g8)
    c: Coincident(g5,g6)
    c: DistanceY(g-10,g0) = 2
    c: DistanceY(g1,g-9) = 2
    c: Coincident(g10,g-6)
    c: Coincident(g11,g10)
    c: Coincident(g12,g10)
    c: Coincident(g13,g-5)
    c: Coincident(g14,g13)
    c: Coincident(g15,g13)
    c: Tangent(g12,g1) = -1.5708
    c: Tangent(g11,g2) = -1.5708
    c: Coincident(g11,g12)
    c: Coincident(g14,g15)
    c: Tangent(g14,g2) = -1.5708
    c: Tangent(g15,g0) = -1.5708
    c: Equal(g10,g13)
    c: Equal(g13,g7)
    c: Equal(g7,g4)
    c: Equal(g12,g6)
    c: DistanceY(g-1,g3) = 18
FEATURE [Sketcher::SketchObject] Sketch027  label="SketchButtonCarve"
  AttachmentOffset = pos=(10,28.6,0) rot=(0,0,1;-0.314159rad)
  FullyConstrained = true
  MapMode = 5
  Placement = pos=(-4.1e-15,10,28.6) rot=(-0.506732,-0.697457,-0.506732;4.35963rad)
  Support = -> [YZ_Plane005]
  expr: .AttachmentOffset.Base.x = <<param>>.button_offset
  expr: .AttachmentOffset.Base.y = <<param>>.button_height - 2
  expr: .AttachmentOffset.Rotation.Angle = <<param>>.button_angle
  expr: .Constraints[12] = <<param>>.button_hole / 2 + 10
  expr: .Constraints[6] = <<param>>.button_hole / 2 + 4
  sketch-geometry (4):
    g0: LineSegment StartX=0 StartY=2 StartZ=0 EndX=12.2 EndY=2 EndZ=0
    g1: ArcOfCircle CenterX=18.2 CenterY=3.09999 CenterZ=0 NormalX=0 NormalY=0 NormalZ=1 AngleXU=0 Radius=6.09999 StartAngle=3.32291 EndAngle=4.71239
    g2: LineSegment StartX=0 StartY=2 StartZ=0 EndX=0 EndY=-3 EndZ=0
    g3: LineSegment StartX=18.2 StartY=-3 StartZ=0 EndX=0 EndY=-3 EndZ=0
  constraints (13):
    c: Horizontal(g0)
    c: Coincident(g1,g0)
    c: Coincident(g2,g0)
    c: Coincident(g3,g1)
    c: Horizontal(g3)
    c: Tangent(g3,g1)
    c: DistanceX(g0,g0) = 12.2
    c: DistanceY(g2,g2) = 5
    c: Coincident(g2,g3)
    c: Vertical(g2)
    c: PointOnObject(g-1,g2)
    c: DistanceY(g2,g-1) = 3
    c: DistanceX(g3,g3) = 18.2
FEATURE [Sketcher::SketchObject] Sketch028  label="SketchTerminals"
  FullyConstrained = true
  MapMode = 5
  Placement = pos=(0,0,0) rot=(1,0,0;1.5708rad)
  Support = -> [XZ_Plane005]
  expr: .Constraints[17] = <<param>>.terminal_thickness
  expr: .Constraints[18] = <<param>>.terminal_height
  expr: .Constraints[21] = <<param>>.bottom_height
  expr: .Constraints[22] = <<param>>.terminal_offset
  expr: .Constraints[23] = <<param>>.terminal_seperation
  sketch-geometry (17):
    g0: LineSegment StartX=10.25 StartY=-12.9 StartZ=0 EndX=11.25 EndY=-12.9 EndZ=0
    g1: LineSegment StartX=11.25 StartY=-12.9 StartZ=0 EndX=11.25 EndY=-19.5 EndZ=0
    g2: LineSegment StartX=11.25 StartY=-19.5 StartZ=0 EndX=10.25 EndY=-19.5 EndZ=0
    g3: LineSegment StartX=10.25 StartY=-19.5 StartZ=0 EndX=10.25 EndY=-17.25 EndZ=0
    g4: LineSegment StartX=-10.25 StartY=-12.9 StartZ=0 EndX=-11.25 EndY=-12.9 EndZ=0
    g5: LineSegment StartX=-11.25 StartY=-12.9 StartZ=0 EndX=-11.25 EndY=-19.5 EndZ=0
    g6: LineSegment StartX=-11.25 StartY=-19.5 StartZ=0 EndX=-10.25 EndY=-19.5 EndZ=0
    g7: LineSegment StartX=-10.25 StartY=-19.5 StartZ=0 EndX=-10.25 EndY=-17.25 EndZ=0
    g8: Circle [constr] CenterX=0 CenterY=-24 CenterZ=0 NormalX=0 NormalY=0 NormalZ=1 AngleXU=0 Radius=3
    g9: LineSegment StartX=-10.25 StartY=-15.15 StartZ=0 EndX=-8.75 EndY=-15.15 EndZ=0
    g10: LineSegment StartX=-8.75 StartY=-15.15 StartZ=0 EndX=-8.75 EndY=-17.25 EndZ=0
    g11: LineSegment StartX=-8.75 StartY=-17.25 StartZ=0 EndX=-10.25 EndY=-17.25 EndZ=0
    g12: LineSegment StartX=-10.25 StartY=-15.15 StartZ=0 EndX=-10.25 EndY=-12.9 EndZ=0
    g13: LineSegment StartX=10.25 StartY=-15.15 StartZ=0 EndX=8.75 EndY=-15.15 EndZ=0
    g14: LineSegment StartX=8.75 StartY=-15.15 StartZ=0 EndX=8.75 EndY=-17.25 EndZ=0
    g15: LineSegment StartX=8.75 StartY=-17.25 StartZ=0 EndX=10.25 EndY=-17.25 EndZ=0
    g16: LineSegment StartX=10.25 StartY=-15.15 StartZ=0 EndX=10.25 EndY=-12.9 EndZ=0
  constraints (48):
    c: Coincident(g0,g1)
    c: Coincident(g1,g2)
    c: Coincident(g2,g3)
    c: Coincident(g16,g0)
    c: Horizontal(g0)
    c: Horizontal(g2)
    c: Vertical(g1)
    c: Vertical(g3)
    c: Coincident(g4,g5)
    c: Coincident(g5,g6)
    c: Coincident(g6,g7)
    c: Coincident(g12,g4)
    c: Horizontal(g4)
    c: Horizontal(g6)
    c: Vertical(g5)
    c: Vertical(g7)
    c: Equal(g4,g0)
    c: DistanceX(g4,g4) = 1
    c: DistanceY(g3,g16) = 6.6
    c: PointOnObject(g8,g-2)
    c: Radius(g8) = 3
    c: DistanceY(g8,g-1) = 24
    c: DistanceY(g8,g1) = 4.5
    c: DistanceX(g6,g1) = 21.5
    c: Symmetric(g4,g0,g-2)
    c: Horizontal(g9)
    c: Coincident(g10,g9)
    c: Vertical(g10)
    c: Coincident(g11,g10)
    c: Horizontal(g11)
    c: Coincident(g7,g11)
    c: Coincident(g12,g9)
    c: Tangent(g7,g12)
    c: Equal(g12,g7)
    c: Horizontal(g5,g1)
    c: DistanceY(g10,g10) = 2.1
    c: DistanceX(g9,g9) = 1.5
    c: Horizontal(g13)
    c: Coincident(g14,g13)
    c: Vertical(g14)
    c: Coincident(g15,g14)
    c: Horizontal(g15)
    c: Coincident(g3,g15)
    c: Coincident(g16,g13)
    c: Tangent(g3,g16)
    c: Equal(g16,g3)
    c: Equal(g13,g9)
    c: Equal(g14,g10)
FEATURE [Sketcher::SketchObject] Sketch029  label="SketchAccess"
  AttachmentOffset = pos=(0,0,-20.5) rot=(0,0,1;0rad)
  FullyConstrained = true
  MapMode = 5
  Placement = pos=(0,0,-20.5) rot=(0,0,1;0rad)
  Support = -> [XY_Plane005]
  expr: .AttachmentOffset.Base.z = -<<param>>.bottom_height + <<param>>.terminal_offset - 1
  expr: .Constraints[19] = <<param>>.mid_depth / 2
  expr: .Constraints[22] = <<param>>.terminal_seperation + <<param>>.terminal_thickness * 2
  expr: .Constraints[23] = <<param>>.terminal_depth
  sketch-geometry (12):
    g0: LineSegment StartX=-11.75 StartY=41 StartZ=0 EndX=-11.75 EndY=18.5 EndZ=0
    g1: LineSegment StartX=-11.75 StartY=18.5 StartZ=0 EndX=-9.25 EndY=18.5 EndZ=0
    g2: LineSegment StartX=-7.95 StartY=21 StartZ=0 EndX=-7.95 EndY=41 EndZ=0
    g3: LineSegment StartX=-7.95 StartY=41 StartZ=0 EndX=-11.75 EndY=41 EndZ=0
    g4: LineSegment StartX=7.95 StartY=41 StartZ=0 EndX=11.75 EndY=41 EndZ=0
    g5: LineSegment StartX=11.75 StartY=41 StartZ=0 EndX=11.75 EndY=18.5 EndZ=0
    g6: LineSegment StartX=11.75 StartY=18.5 StartZ=0 EndX=9.25 EndY=18.5 EndZ=0
    g7: LineSegment StartX=7.95 StartY=21 StartZ=0 EndX=7.95 EndY=41 EndZ=0
    g8: LineSegment StartX=9.25 StartY=18.5 StartZ=0 EndX=9.25 EndY=19.5 EndZ=0
    g9: LineSegment StartX=7.95 StartY=21 StartZ=0 EndX=9.25 EndY=19.5 EndZ=0
    g10: LineSegment StartX=-9.25 StartY=18.5 StartZ=0 EndX=-9.25 EndY=19.5 EndZ=0
    g11: LineSegment StartX=-9.25 StartY=19.5 StartZ=0 EndX=-7.95 EndY=21 EndZ=0
  constraints (35):
    c: Vertical(g0)
    c: Coincident(g0,g1)
    c: Vertical(g2)
    c: Coincident(g2,g3)
    c: Coincident(g3,g0)
    c: Horizontal(g3)
    c: Horizontal(g4)
    c: Coincident(g4,g5)
    c: Vertical(g5)
    c: Coincident(g5,g6)
    c: Horizontal(g6)
    c: Coincident(g7,g4)
    c: Vertical(g7)
    c: Equal(g3,g4)
    c: Equal(g0,g5)
    c: Horizontal(g1)
    c: Equal(g2,g7)
    c: Equal(g1,g6)
    c: Symmetric(g2,g4,g-2)
    c: DistanceY(g-1,g0) = 41
    c: DistanceX(g1,g1) = 2.5
    c: DistanceX(g0,g2) = 3.8
    c: DistanceX(g0,g5) = 23.5
    c: DistanceY(g5,g4) = 22.5
    c: DistanceY(g2,g2) = 20
    c: Coincident(g8,g6) = 23.5
    c: Vertical(g8) = 22
    c: Coincident(g9,g7)
    c: Coincident(g9,g8)
    c: Coincident(g10,g1)
    c: Coincident(g11,g10)
    c: Coincident(g11,g2)
    c: Equal(g8,g10)
    c: DistanceY(g8,g8) = 1
    c: Vertical(g10)
FEATURE [Sketcher::SketchObject] Sketch030  label="SketchFront"
  AttachmentOffset = pos=(0,0,41) rot=(0,0,1;0rad)
  FullyConstrained = true
  MapMode = 5
  Placement = pos=(0,-41,-9.1e-15) rot=(1,0,0;1.5708rad)
  Support = -> [XZ_Plane006]
  expr: .AttachmentOffset.Base.z = <<param>>.mid_depth / 2
  expr: .Constraints[10] = <<param>>.front_width2
  expr: .Constraints[11] = <<param>>.front_width2
  expr: .Constraints[12] = <<param>>.front_height + 2
  expr: .Constraints[22] = <<param>>.radius_big * 1.2
  expr: .Constraints[27] = <<param>>.radius_big
  expr: .Constraints[6] = <<param>>.radius_small
  expr: .Constraints[7] = <<param>>.bottom_width
  expr: .Constraints[9] = <<param>>.bottom_height
  sketch-geometry (12):
    g0: LineSegment StartX=-47.5 StartY=48 StartZ=0 EndX=47.5 EndY=48 EndZ=0
    g1: LineSegment StartX=47.5 StartY=48 StartZ=0 EndX=47.5 EndY=9.54506 EndZ=0
    g2: LineSegment StartX=36 StartY=-9.78755 StartZ=0 EndX=36 EndY=-21 EndZ=0
    g3: LineSegment StartX=33 StartY=-24 StartZ=0 EndX=-33 EndY=-24 EndZ=0
    g4: LineSegment StartX=-36 StartY=-21 StartZ=0 EndX=-36 EndY=-9.78755 EndZ=0
    g5: LineSegment StartX=-47.5 StartY=9.54506 StartZ=0 EndX=-47.5 EndY=48 EndZ=0
    g6: ArcOfCircle CenterX=-33 CenterY=-21 CenterZ=0 NormalX=0 NormalY=0 NormalZ=1 AngleXU=0 Radius=3 StartAngle=3.14159 EndAngle=4.71239
    g7: ArcOfCircle CenterX=33 CenterY=-21 CenterZ=0 NormalX=0 NormalY=0 NormalZ=1 AngleXU=0 Radius=3 StartAngle=4.71239 EndAngle=6.28319
    g8: ArcOfCircle CenterX=46 CenterY=-9.78755 CenterZ=0 NormalX=0 NormalY=0 NormalZ=1 AngleXU=0 Radius=10 StartAngle=2.06834 EndAngle=3.14159
    g9: ArcOfCircle CenterX=35.5 CenterY=9.54506 CenterZ=0 NormalX=0 NormalY=0 NormalZ=1 AngleXU=0 Radius=12 StartAngle=5.20994 EndAngle=6.28319
    g10: ArcOfCircle CenterX=-46 CenterY=-9.78755 CenterZ=0 NormalX=0 NormalY=0 NormalZ=1 AngleXU=0 Radius=10 StartAngle=0 EndAngle=1.07325
    g11: ArcOfCircle CenterX=-35.5 CenterY=9.54506 CenterZ=0 NormalX=0 NormalY=0 NormalZ=1 AngleXU=0 Radius=12 StartAngle=3.14159 EndAngle=4.21484
  constraints (30):
    c: Vertical(g2)
    c: Vertical(g4)
    c: Tangent(g4,g6) = 1.5708
    c: Tangent(g3,g6) = 1.5708
    c: Tangent(g3,g7) = 1.5708
    c: Tangent(g2,g7) = 1.5708
    c: Radius(g7) = 3
    c: DistanceX(g4,g2) = 72
    c: Symmetric(g3,g3,g-2)
    c: DistanceY(g3,g-1) = 24
    c: DistanceX(g5,g1) = 95
    c: DistanceX(g5,g1) = 95
    c: DistanceY(g3,g0) = 72
    c: Equal(g7,g6)
    c: Equal(g10,g8)
    c: Symmetric(g5,g1,g-2)
    c: Equal(g4,g2)
    c: Coincident(g8,g2)
    c: Coincident(g0,g1)
    c: Coincident(g5,g0)
    c: Symmetric(g0,g0,g-2)
    c: Equal(g9,g11)
    c: Radius(g9) = 12
    c: Tangent(g11,g5) = 1.5708
    c: Tangent(g1,g9) = 1.5708
    c: Tangent(g11,g10) = 1.5708
    c: Tangent(g8,g9) = 1.5708
    c: Radius(g8) = 10
    c: DistanceY(g8,g-1) = 1
    c: Tangent(g10,g4) = -1.5708
FEATURE [Sketcher::SketchObject] Sketch031  label="SketchRear"
  AttachmentOffset = pos=(0,0,-46) rot=(0,0,1;0rad)
  FullyConstrained = true
  MapMode = 5
  Placement = pos=(0,46,1.02e-14) rot=(1,0,0;1.5708rad)
  Support = -> [XZ_Plane006]
  expr: .AttachmentOffset.Base.z = -<<param>>.mid_depth / 2 - <<param>>.back_thickness
  expr: .Constraints[15] = <<param>>.front_height + 2
  expr: .Constraints[1] = <<param>>.radius_small
  expr: .Constraints[2] = <<param>>.bottom_height
  expr: .Constraints[3] = <<param>>.rear_width
  sketch-geometry (6):
    g0: LineSegment StartX=-33 StartY=-24 StartZ=0 EndX=33 EndY=-24 EndZ=0
    g1: LineSegment StartX=36 StartY=48 StartZ=0 EndX=-36 EndY=48 EndZ=0
    g2: ArcOfCircle CenterX=-33 CenterY=-21 CenterZ=0 NormalX=0 NormalY=0 NormalZ=1 AngleXU=0 Radius=3 StartAngle=3.14159 EndAngle=4.71239
    g3: ArcOfCircle CenterX=33 CenterY=-21 CenterZ=0 NormalX=0 NormalY=0 NormalZ=1 AngleXU=0 Radius=3 StartAngle=4.71239 EndAngle=6.28319
    g4: LineSegment StartX=36 StartY=-21 StartZ=0 EndX=36 EndY=48 EndZ=0
    g5: LineSegment StartX=-36 StartY=-21 StartZ=0 EndX=-36 EndY=48 EndZ=0
  constraints (19):
    c: Horizontal(g0)
    c: Radius(g3) = 3
    c: DistanceY(g0,g-1) = 24
    c: DistanceX(g2,g3) = 72
    c: Coincident(g4,g3)
    c: Vertical(g4)
    c: Coincident(g5,g2)
    c: Equal(g5,g4)
    c: Horizontal(g3,g3)
    c: Horizontal(g2,g2)
    c: Equal(g2,g3)
    c: Coincident(g0,g2)
    c: Coincident(g0,g3)
    c: Vertical(g2,g0)
    c: Vertical(g5)
    c: DistanceY(g0,g1) = 72
    c: Symmetric(g4,g5,g-2)
    c: Coincident(g4,g1)
    c: Coincident(g5,g1)
FEATURE [Part::Plane] Plane002  label="Plane"
  AttacherType = Attacher::AttachEngine3D
  Length = 152
  Placement = pos=(-75,41,-75) rot=(1,0,0;1.5708rad)
  Support = -> [XZ_Plane006]
  Width = 150
  expr: .Placement.Base.y = <<param>>.mid_depth / 2
FEATURE [Sketcher::SketchObject] Sketch032  label="SketchBack"
  FullyConstrained = true
  MapMode = 5
  Placement = pos=(0,0,0) rot=(1,0,0;1.5708rad)
  Support = -> [XZ_Plane]
  expr: .Constraints[10] = <<param>>.rear_screw_width1
  expr: .Constraints[11] = <<param>>.reart_screw_width2
  expr: .Constraints[12] = <<param>>.rear_screw_height
  expr: .Constraints[15] = <<param>>.rear_screw_offset
  expr: .Constraints[1] = <<param>>.bottom_height
  expr: .Constraints[2] = <<param>>.rear_width
  expr: .Constraints[9] = <<param>>.screw_hole + 1
  sketch-geometry (6):
    g0: LineSegment [constr] StartX=36 StartY=-24 StartZ=0 EndX=-36 EndY=-24 EndZ=0
    g1: Circle CenterX=-29 CenterY=14.9 CenterZ=0 NormalX=0 NormalY=0 NormalZ=1 AngleXU=0 Radius=1.75
    g2: Circle CenterX=0 CenterY=14.9 CenterZ=0 NormalX=0 NormalY=0 NormalZ=1 AngleXU=0 Radius=1.75
    g3: Circle CenterX=29 CenterY=14.9 CenterZ=0 NormalX=0 NormalY=0 NormalZ=1 AngleXU=0 Radius=1.75
    g4: Circle CenterX=-27.5 CenterY=-16.6 CenterZ=0 NormalX=0 NormalY=0 NormalZ=1 AngleXU=0 Radius=1.75
    g5: Circle CenterX=27.5 CenterY=-16.6 CenterZ=0 NormalX=0 NormalY=0 NormalZ=1 AngleXU=0 Radius=1.75
  constraints (16):
    c: Symmetric(g0,g0,g-2)
    c: DistanceY(g0,g-1) = 24
    c: DistanceX(g0,g0) = 72
    c: Symmetric(g1,g3,g-2)
    c: Symmetric(g4,g5,g-2)
    c: Equal(g4,g1)
    c: Equal(g1,g2)
    c: Equal(g2,g3)
    c: Equal(g3,g5)
    c: Diameter(g1) = 3.5
    c: DistanceX(g1,g3) = 58
    c: DistanceX(g4,g5) = 55
    c: DistanceY(g5,g3) = 31.5
    c: Horizontal(g1,g2)
    c: PointOnObject(g2,g-2)
    c: DistanceY(g0,g5) = 7.4
FEATURE [Part::Loft] Loft
  Closed = false
  MaxDegree = 5
  Ruled = false
  Sections = -> [Sketch030,Sketch031]
  Solid = true
FEATURE [Part::Extrusion] Extrude
  Base = -> Sketch012
  Dir = (1,-1e-16,1e-16)
  DirMode = 2
  FaceMakerClass = Part::FaceMakerBullseye
  InnerTaperAngle = 0
  InnerTaperAngleRev = 0
  LengthFwd = 100
  LengthRev = 0
  Solid = true
  Symmetric = true
FEATURE [Part::MultiCommon] Common
  Shapes = -> [Extrude,Loft]
FEATURE [Part::FeaturePython] Slice  # WARN: FeaturePython — macro-defined, semantics opaque (R4)
  Base = -> Common
  Mode = 1
  Tolerance = 0
  Tools = -> [Plane002]
FEATURE [Part::FeaturePython] Slice_child0  label="Slice.0"  # WARN: FeaturePython — macro-defined, semantics opaque (R4)
  Base = -> Slice
  FilterType = 1
  Invert = false
  OverrideMaxVal = 0
  WindowFrom = 80
  WindowTo = 100
  items = 0
FEATURE [Part::FeaturePython] Slice_child1  label="Slice.1"  # WARN: FeaturePython — macro-defined, semantics opaque (R4)
  Base = -> Slice
  FilterType = 1
  Invert = false
  OverrideMaxVal = 0
  WindowFrom = 80
  WindowTo = 100
  items = 1
FEATURE [App::DocumentObjectGroup] GrExplode_Slice  label="Exploded Slice"
  ExportMode = 1
  Group = -> [Slice_child0,Slice_child1]
  _GroupVersion = 1
FEATURE [App::DocumentObjectGroup] Group001  label="BaseShape"
  ExportMode = 1
  Group = -> [Common,Sketch012,Sketch031,Sketch030,Plane002,GrExplode_Slice]
  _GroupVersion = 1
FEATURE [PartDesign::FeatureBase] BaseFeature
  BaseFeature = -> Slice_child1
  NewSolid = false
  Suppress = false
FEATURE [PartDesign::Pocket] Pocket
  BaseFeature = -> BaseFeature
  ClaimChildren = false
  Fit = 0
  FitJoin = 0
  InnerFit = 0
  InnerFitJoin = 0
  InnerTaperAngle = 0
  InnerTaperAngleRev = 0
  Length = 5
  Length2 = 100
  Midplane = true
  NewSolid = false
  Profile = -> Sketch032
  Suppress = false
  Type = 1
FEATURE [PartDesign::FeatureBase] BaseFeature001
  BaseFeature = -> Slice_child0
  NewSolid = false
  Suppress = false
FEATURE [PartDesign::Pocket] Pocket001  label="PocketBatt"
  BaseFeature = -> BaseFeature001
  ClaimChildren = false
  Fit = 0
  FitJoin = 0
  InnerFit = 0
  InnerFitJoin = 0
  InnerTaperAngle = 0
  InnerTaperAngleRev = 0
  Length = 14.6
  Length2 = 100
  NewSolid = false
  Profile = -> Sketch018
  Reversed = true
  Suppress = false
  Type = 0
  expr: Length = <<param>>.batt_carveout
FEATURE [PartDesign::Pad] Pad  label="PadBatt"
  BaseFeature = -> Pocket001
  ClaimChildren = false
  Direction = (1,1,1)
  Fit = 0
  FitJoin = 0
  InnerFit = 0
  InnerFitJoin = 0
  InnerTaperAngle = 0
  InnerTaperAngleRev = 0
  Length = 45
  Length2 = 100
  NewSolid = false
  Profile = -> Sketch019
  Suppress = false
  Type = 0
  expr: Length = <<param>>.batt_rail_length
FEATURE [PartDesign::Pocket] Pocket002  label="PocketSupport"
  BaseFeature = -> Pad
  ClaimChildren = false
  Fit = 0
  FitJoin = 0
  InnerFit = 0
  InnerFitJoin = 0
  InnerTaperAngle = 0
  InnerTaperAngleRev = 0
  Length = 5
  Length2 = 100
  NewSolid = false
  Profile = -> Sketch
  Suppress = false
  Type = 0
FEATURE [PartDesign::Pocket] Pocket006  label="PocketTerminal"
  BaseFeature = -> Pocket002
  ClaimChildren = false
  Fit = 0
  FitJoin = 0
  InnerFit = 0
  InnerFitJoin = 0
  InnerTaperAngle = 0
  InnerTaperAngleRev = 0
  Length = 18.5
  Length2 = 100
  NewSolid = false
  Profile = -> Sketch028
  Suppress = false
  Type = 0
  expr: Length = <<param>>.mid_depth / 2 - <<param>>.terminal_depth
FEATURE [PartDesign::Pocket] Pocket005  label="PocketAccess"
  BaseFeature = -> Pocket006
  ClaimChildren = false
  Fit = 0
  FitJoin = 0
  InnerFit = 0
  InnerFitJoin = 0
  InnerTaperAngle = 0
  InnerTaperAngleRev = 0
  Length = 22.5
  Length2 = 100
  NewSolid = false
  Profile = -> Sketch029
  Reversed = true
  Suppress = false
  Type = 0
  expr: Length = <<param>>.terminal_depth
FEATURE [Sketcher::SketchObject] Sketch033  label="SketchFace"
  FullyConstrained = true
  MapMode = 5
  Placement = pos=(0,0,0) rot=(1,0,0;1.5708rad)
  Support = -> [XZ_Plane007]
  expr: .Constraints[12] = <<param>>.face_radius
  expr: .Constraints[21] = <<param>>.face_width1 - 0.4
  expr: .Constraints[22] = <<param>>.face_width2 - 0.4
  expr: .Constraints[23] = <<param>>.face_height - 0.4
  expr: .Constraints[27] = <<param>>.screw_hole + 1
  expr: .Constraints[28] = <<param>>.front_screw_width2 / 2
  expr: .Constraints[29] = <<param>>.front_screw_width2 / 2
  expr: .Constraints[30] = <<param>>.front_screw_width1 / 2
  expr: .Constraints[31] = <<param>>.front_screw_width1 / 2
  expr: .Constraints[32] = <<param>>.front_screw_height
  expr: .Constraints[35] = <<param>>.front_screw_offset + <<param>>.face_offset
  expr: .Constraints[48] = <<param>>.face_offset
  sketch-geometry (23):
    g0: LineSegment StartX=-34.3037 StartY=43.4 StartZ=0 EndX=34.3037 EndY=43.4 EndZ=0
    g1: LineSegment StartX=42.3 StartY=35.6438 StartZ=0 EndX=43.05 EndY=11.0438 EndZ=0
    g2: LineSegment StartX=35.0537 StartY=2.8 StartZ=0 EndX=-35.0537 EndY=2.8 EndZ=0
    g3: LineSegment StartX=-43.05 StartY=11.0438 StartZ=0 EndX=-42.3 EndY=35.6438 EndZ=0
    g4: ArcOfCircle CenterX=34.3037 CenterY=35.4 CenterZ=0 NormalX=0 NormalY=0 NormalZ=1 AngleXU=0 Radius=8 StartAngle=0.0304753 EndAngle=1.5708
    g5: ArcOfCircle CenterX=35.0537 CenterY=10.8 CenterZ=0 NormalX=0 NormalY=0 NormalZ=1 AngleXU=0 Radius=8 StartAngle=4.71239 EndAngle=6.31366
    g6: ArcOfCircle CenterX=-34.3037 CenterY=35.4 CenterZ=0 NormalX=0 NormalY=0 NormalZ=1 AngleXU=0 Radius=8 StartAngle=1.5708 EndAngle=3.11112
    g7: ArcOfCircle CenterX=-35.0537 CenterY=10.8 CenterZ=0 NormalX=0 NormalY=0 NormalZ=1 AngleXU=0 Radius=8 StartAngle=3.11111 EndAngle=4.71239
    g8: Circle CenterX=-36.75 CenterY=38.3 CenterZ=0 NormalX=0 NormalY=0 NormalZ=1 AngleXU=0 Radius=1.75
    g9: Circle CenterX=36.75 CenterY=38.3 CenterZ=0 NormalX=0 NormalY=0 NormalZ=1 AngleXU=0 Radius=1.75
    g10: Circle CenterX=-38 CenterY=8.3 CenterZ=0 NormalX=0 NormalY=0 NormalZ=1 AngleXU=0 Radius=1.75
    g11: Circle CenterX=38 CenterY=8.3 CenterZ=0 NormalX=0 NormalY=0 NormalZ=1 AngleXU=0 Radius=1.75
    g12: LineSegment StartX=-14 StartY=33.75 StartZ=0 EndX=14 EndY=33.75 EndZ=0
    g13: LineSegment StartX=16 StartY=31.75 StartZ=0 EndX=16 EndY=19.25 EndZ=0
    g14: LineSegment StartX=14 StartY=17.25 StartZ=0 EndX=-14 EndY=17.25 EndZ=0
    g15: LineSegment StartX=-16 StartY=19.25 StartZ=0 EndX=-16 EndY=31.75 EndZ=0
    g16: ArcOfCircle CenterX=-14 CenterY=31.75 CenterZ=0 NormalX=0 NormalY=0 NormalZ=1 AngleXU=0 Radius=2 StartAngle=1.5708 EndAngle=3.14159
    g17: ArcOfCircle CenterX=-14 CenterY=19.25 CenterZ=0 NormalX=0 NormalY=0 NormalZ=1 AngleXU=0 Radius=2 StartAngle=3.14159 EndAngle=4.71239
    g18: ArcOfCircle CenterX=14 CenterY=19.25 CenterZ=0 NormalX=0 NormalY=0 NormalZ=1 AngleXU=0 Radius=2 StartAngle=4.71239 EndAngle=6.28319
    g19: ArcOfCircle CenterX=14 CenterY=31.75 CenterZ=0 NormalX=0 NormalY=0 NormalZ=1 AngleXU=0 Radius=2 StartAngle=7e-16 EndAngle=1.5708
    g20: Circle CenterX=-31 CenterY=21.5 CenterZ=0 NormalX=0 NormalY=0 NormalZ=1 AngleXU=0 Radius=7.75
    g21: Circle CenterX=31 CenterY=25.5 CenterZ=0 NormalX=0 NormalY=0 NormalZ=1 AngleXU=0 Radius=3.6
    g22: LineSegment [constr] StartX=-69 StartY=25.5 StartZ=0 EndX=31 EndY=25.5 EndZ=0
  constraints (67):
    c: Coincident(g4,g0)
    c: Coincident(g4,g1)
    c: Coincident(g5,g1)
    c: Coincident(g5,g2)
    c: Coincident(g6,g0)
    c: Coincident(g6,g3)
    c: Coincident(g7,g3)
    c: Coincident(g7,g2)
    c: Equal(g1,g3)
    c: Equal(g4,g6)
    c: Equal(g6,g7)
    c: Equal(g7,g5)
    c: Radius(g4) = 8
    c: Tangent(g6,g3)
    c: Tangent(g7,g3)
    c: Tangent(g7,g2)
    c: Tangent(g6,g0)
    c: Tangent(g4,g0)
    c: Tangent(g4,g1)
    c: Tangent(g5,g1)
    c: Tangent(g5,g2)
    c: DistanceX(g3,g1) = 84.6
    c: DistanceX(g3,g1) = 86.1
    c: DistanceY(g2,g0) = 40.6
    c: Equal(g9,g8)
    c: Equal(g8,g10)
    c: Equal(g10,g11)
    c: Diameter(g8) = 3.5
    c: DistanceX(g10,g-1) = 38
    c: DistanceX(g-1,g11) = 38
    c: DistanceX(g-1,g9) = 36.75
    c: DistanceX(g8,g-1) = 36.75
    c: DistanceY(g11,g9) = 30
    c: Horizontal(g8,g9)
    c: Horizontal(g10,g11)
    c: DistanceY(g-1,g11) = 8.3
    c: Horizontal(g12)
    c: Horizontal(g14)
    c: Vertical(g13)
    c: Vertical(g15)
    c: Tangent(g15,g16) = 1.5708
    c: Tangent(g12,g16) = 1.5708
    c: Tangent(g15,g17) = 1.5708
    c: Tangent(g14,g17) = 1.5708
    c: Tangent(g14,g18) = 1.5708
    c: Tangent(g13,g18) = 1.5708
    c: Tangent(g12,g19) = 1.5708
    c: Tangent(g13,g19) = 1.5708
    c: DistanceY(g-1,g2) = 2.8
    c: Horizontal(g0)
    c: Symmetric(g2,g2,g-2)
    c: Diameter(g20) = 15.5
    c: Diameter(g21) = 7.2
    c: Equal(g16,g17)
    c: Equal(g17,g18)
    c: Equal(g18,g19)
    c: DistanceY(g14,g12) = 16.5
    c: DistanceX(g15,g13) = 32
    c: Radius(g19) = 2
    c: DistanceX(g20,g21) = 62
    c: DistanceX(g13,g21) = 15
    c: Symmetric(g12,g14,g22)
    c: DistanceY(g20,g22) = 4
    c: DistanceY(g-1,g22) = 25.5
    c: DistanceX(g-1,g21) = 31
    c: DistanceX(g22,g22) = 100
    c: Coincident(g22,g21)
FEATURE [PartDesign::Pad] Pad001  label="PadFace"
  ClaimChildren = false
  Direction = (1,1,1)
  Fit = 0
  FitJoin = 0
  InnerFit = 0
  InnerFitJoin = 0
  InnerTaperAngle = 0
  InnerTaperAngleRev = 0
  Length = 3
  Length2 = 100
  NewSolid = false
  Placement = pos=(0,0,0) rot=(1,0,0;1.5708rad)
  Profile = -> Sketch033
  Suppress = false
  Type = 0
  expr: Length = <<param>>.face_thickness
FEATURE [PartDesign::Chamfer] Chamfer001
  Angle = 45
  Base = -> Pad001 [Edge34]
  BaseFeature = -> Pad001
  ChamferType = 0
  FlipDirection = false
  NewSolid = false
  Placement = pos=(0,0,0) rot=(1,0,0;1.5708rad)
  Size = 2
  Size2 = 1
  SupportTransform = false
  Suppress = false
FEATURE [PartDesign::Chamfer] Chamfer002
  Angle = 45
  Base = -> Chamfer001 [Edge54,Edge56,Edge53,Edge55]
  BaseFeature = -> Chamfer001
  ChamferType = 0
  FlipDirection = false
  NewSolid = false
  Placement = pos=(0,0,0) rot=(1,0,0;1.5708rad)
  Size = 1.4
  Size2 = 1
  SupportTransform = false
  Suppress = false
FEATURE [Sketcher::SketchObject] Sketch034
  FullyConstrained = true
  MapMode = 5
  Placement = pos=(0,0,0) rot=(1,0,0;1.5708rad)
  Support = -> [XZ_Plane008]
  sketch-geometry (6):
    g0: LineSegment StartX=-1 StartY=6.25 StartZ=0 EndX=1 EndY=6.25 EndZ=0
    g1: LineSegment StartX=1 StartY=6.25 StartZ=0 EndX=1 EndY=7.75 EndZ=0
    g2: LineSegment StartX=1 StartY=7.75 StartZ=0 EndX=0 EndY=7.75 EndZ=0
    g3: LineSegment StartX=0 StartY=7.75 StartZ=0 EndX=0 EndY=8.75 EndZ=0
    g4: LineSegment StartX=0 StartY=8.75 StartZ=0 EndX=-1 EndY=8.75 EndZ=0
    g5: LineSegment StartX=-1 StartY=8.75 StartZ=0 EndX=-1 EndY=6.25 EndZ=0
  constraints (17):
    c: Coincident(g0,g1)
    c: Vertical(g1)
    c: Coincident(g1,g2)
    c: Horizontal(g2)
    c: Coincident(g2,g3)
    c: Vertical(g3)
    c: Coincident(g3,g4)
    c: Horizontal(g4)
    c: Coincident(g4,g5)
    c: Coincident(g5,g0)
    c: Vertical(g5)
    c: DistanceX(g0,g0) = 2
    c: DistanceY(g3,g3) = 1
    c: DistanceX(g4,g4) = 1
    c: Symmetric(g0,g0,g-2)
    c: DistanceY(g-1,g0) = 6.25
    c: DistanceY(g5,g5) = 2.5
FEATURE [PartDesign::Revolution] Revolution001
  Angle = 360
  Axis = (1,0,0)
  Base = (0,0,0)
  ClaimChildren = false
  Fit = 0
  FitJoin = 0
  InnerFit = 0
  InnerFitJoin = 0
  NewSolid = false
  Placement = pos=(0,0,0) rot=(1,0,0;1.5708rad)
  Profile = -> Sketch034
  ReferenceAxis = -> X_Axis008
  Suppress = false
FEATURE [PartDesign::Body] Body006  label="BodyRing"
  AutoGroupSolids = false
  ExportMode = 0
  Group = -> [Sketch034,Revolution001]
  Origin = -> Origin008
  Tip = -> Revolution001
  _ExportChildren = -> [Revolution001]
  _GroupVersion = 1
FEATURE [Part::Box] Box  label="Cube"
  AttacherType = Attacher::AttachEngine3D
  Height = 18
  Length = 18
  Placement = pos=(-9,-0.25,-9) rot=(0,0,1;0rad)
  Width = 0.5
FEATURE [Part::FeaturePython] Slice001  # WARN: FeaturePython — macro-defined, semantics opaque (R4)
  Base = -> Body006
  Mode = 1
  Tolerance = 0
  Tools = -> [Box]
FEATURE [Part::FeaturePython] Slice001_child1  label="Slice001.1"  # WARN: FeaturePython — macro-defined, semantics opaque (R4)
  Base = -> Slice001
  FilterType = 1
  Invert = false
  OverrideMaxVal = 0
  WindowFrom = 80
  WindowTo = 100
  items = 1
FEATURE [Part::FeaturePython] Slice001_child2  label="Slice001.2"  # WARN: FeaturePython — macro-defined, semantics opaque (R4)
  Base = -> Slice001
  FilterType = 1
  Invert = false
  OverrideMaxVal = 0
  WindowFrom = 80
  WindowTo = 100
  items = 2
FEATURE [App::DocumentObjectGroup] GrExplode_Slice001  label="Exploded SliceRing"
  ExportMode = 1
  Group = -> [Slice001_child1,Slice001_child2]
  _GroupVersion = 1
FEATURE [Sketcher::SketchObject] Sketch035
  AttachmentOffset = pos=(0,0,1.5) rot=(1,0,0;0rad)
  ExternalGeometry = -> [Sketch033]
  FullyConstrained = true
  MapMode = 5
  Placement = pos=(0,-1.5,-3e-16) rot=(1,0,0;1.5708rad)
  Support = -> [XZ_Plane007]
  expr: .AttachmentOffset.Base.z = <<param>>.face_thickness - 1.5
  sketch-geometry (1):
    g0: Circle CenterX=-31 CenterY=21.5 CenterZ=0 NormalX=0 NormalY=0 NormalZ=1 AngleXU=0 Radius=9
  constraints (2):
    c: Coincident(g0,g-3)
    c: Diameter(g0) = 18
FEATURE [PartDesign::Pocket] Pocket008
  BaseFeature = -> Chamfer002
  ClaimChildren = false
  Fit = 0
  FitJoin = 0
  InnerFit = 0
  InnerFitJoin = 0
  InnerTaperAngle = 0
  InnerTaperAngleRev = 0
  Length = 1.5
  Length2 = 100
  NewSolid = false
  Placement = pos=(0,0,0) rot=(1,0,0;1.5708rad)
  Profile = -> Sketch035
  Reversed = true
  Suppress = false
  Type = 1
FEATURE [Mesh::Feature] Mesh002  label="Exploded Slice001 (Meshed)"
FEATURE [Sketcher::SketchObject] Sketch036
  ExternalGeometry = -> [Sketch033]
  FullyConstrained = true
  MapMode = 5
  Placement = pos=(0,0,0) rot=(1,0,0;1.5708rad)
  Support = -> [XZ_Plane007]
  sketch-geometry (5):
    g0: ArcOfCircle CenterX=30 CenterY=19.5 CenterZ=0 NormalX=0 NormalY=0 NormalZ=1 AngleXU=0 Radius=0.75 StartAngle=1.5708 EndAngle=4.71239
    g1: ArcOfCircle CenterX=32 CenterY=19.5 CenterZ=0 NormalX=0 NormalY=0 NormalZ=1 AngleXU=0 Radius=0.75 StartAngle=4.71239 EndAngle=7.85398
    g2: LineSegment StartX=30 StartY=18.75 StartZ=0 EndX=32 EndY=18.75 EndZ=0
    g3: LineSegment StartX=30 StartY=20.25 StartZ=0 EndX=32 EndY=20.25 EndZ=0
    g4: LineSegment [constr] StartX=31 StartY=25.5 StartZ=0 EndX=31 EndY=16.5 EndZ=0
  constraints (12):
    c: Tangent(g0,g3) = 1.5708
    c: Tangent(g0,g2) = -1.5708
    c: Tangent(g2,g1) = -1.5708
    c: Tangent(g3,g1) = 1.5708
    c: Horizontal(g2)
    c: Equal(g0,g1)
    c: DistanceY(g1,g-3) = 6
    c: DistanceY(g1,g1) = 1.5
    c: DistanceX(g0,g1) = 2
    c: Coincident(g4,g-3)
    c: Symmetric(g0,g1,g4)
    c: DistanceY(g4,g4) = 9
FEATURE [PartDesign::Pocket] Pocket009
  BaseFeature = -> Pocket008
  ClaimChildren = false
  Fit = 0
  FitJoin = 0
  InnerFit = 0
  InnerFitJoin = 0
  InnerTaperAngle = 0
  InnerTaperAngleRev = 0
  Length = 1
  Length2 = 100
  NewSolid = false
  Placement = pos=(0,0,0) rot=(1,0,0;1.5708rad)
  Profile = -> Sketch036
  Reversed = true
  Suppress = false
  Type = 0
FEATURE [PartDesign::Body] Body005  label="BodyKSGER"
  AutoGroupSolids = false
  ExportMode = 0
  Group = -> [Sketch033,Pad001,Chamfer001,Chamfer002,Sketch035,Pocket008,Sketch036,Pocket009]
  Origin = -> Origin007
  Tip = -> Pocket009
  _ExportChildren = -> [Pad001,Chamfer001,Chamfer002,Pocket008,Pocket009]
  _GroupVersion = 1
FEATURE [Mesh::Feature] Mesh003  label="BodyKSGER (Meshed)"
FEATURE [PartDesign::Fillet] Fillet
  Base = -> Pocket [Edge63,Edge30]
  BaseFeature = -> Pocket
  NewSolid = false
  Radius = 10
  SupportTransform = false
  Suppress = false
  expr: Radius = <<param>>.radius_big
FEATURE [PartDesign::Fillet] Fillet004
  Base = -> Fillet [Edge4]
  BaseFeature = -> Fillet
  NewSolid = false
  Radius = 2.9
  SupportTransform = false
  Suppress = false
FEATURE [PartDesign::Chamfer] Chamfer
  Angle = 45
  Base = -> Fillet004 [Edge9,Edge10,Edge11,Edge25,Edge26]
  BaseFeature = -> Fillet004
  ChamferType = 0
  FlipDirection = false
  NewSolid = false
  Size = 1.4
  Size2 = 1
  SupportTransform = false
  Suppress = false
FEATURE [PartDesign::Body] Body  label="BodyBack"
  AutoGroupSolids = false
  BaseFeature = -> Slice_child1
  ExportMode = 0
  Group = -> [BaseFeature,Sketch032,Pocket,Fillet,Fillet004,Chamfer]
  Origin = -> Origin
  Tip = -> Chamfer
  _ExportChildren = -> [BaseFeature,Pocket,Fillet,Fillet004,Chamfer]
  _GroupVersion = 1
FEATURE [Sketcher::SketchObject] Sketch037
  AttachmentOffset = pos=(0,0,-41) rot=(0,0,1;0rad)
  FullyConstrained = true
  MapMode = 5
  Placement = pos=(0,41,9.1e-15) rot=(1,0,0;1.5708rad)
  Support = -> [XZ_Plane005]
  expr: .AttachmentOffset.Base.z = -<<param>>.mid_depth / 2
  expr: .Constraints[20] = <<param>>.reart_screw_width2
  expr: .Constraints[23] = <<param>>.screw_hole / 2
  expr: .Constraints[24] = <<param>>.rear_screw_offset
  expr: .Constraints[2] = <<param>>.bottom_height
  sketch-geometry (9):
    g0: Circle [constr] CenterX=0 CenterY=-24 CenterZ=0 NormalX=0 NormalY=0 NormalZ=1 AngleXU=0 Radius=3
    g1: LineSegment StartX=4.5 StartY=-22.8 StartZ=0 EndX=4.5 EndY=-24 EndZ=0
    g2: LineSegment StartX=4.5 StartY=-24 StartZ=0 EndX=11.5 EndY=-24 EndZ=0
    g3: LineSegment StartX=11.5 StartY=-24 StartZ=0 EndX=11.5 EndY=-22.8 EndZ=0
    g4: ArcOfCircle CenterX=5.5 CenterY=-22.8 CenterZ=0 NormalX=0 NormalY=0 NormalZ=1 AngleXU=0 Radius=1 StartAngle=1.5708 EndAngle=3.14159
    g5: ArcOfCircle CenterX=10.5 CenterY=-22.8 CenterZ=0 NormalX=0 NormalY=0 NormalZ=1 AngleXU=0 Radius=1 StartAngle=-9e-16 EndAngle=1.5708
    g6: LineSegment StartX=5.5 StartY=-21.8 StartZ=0 EndX=10.5 EndY=-21.8 EndZ=0
    g7: Circle CenterX=-27.5 CenterY=-16.6 CenterZ=0 NormalX=0 NormalY=0 NormalZ=1 AngleXU=0 Radius=1.25
    g8: Circle CenterX=27.5 CenterY=-16.6 CenterZ=0 NormalX=0 NormalY=0 NormalZ=1 AngleXU=0 Radius=1.25
  constraints (25):
    c: PointOnObject(g0,g-2)
    c: Radius(g0) = 3
    c: DistanceY(g0,g-1) = 24
    c: Vertical(g1)
    c: Coincident(g1,g2)
    c: Horizontal(g2)
    c: Coincident(g2,g3)
    c: Coincident(g5,g3)
    c: Horizontal(g6)
    c: Vertical(g3)
    c: Horizontal(g0,g1)
    c: DistanceX(g0,g1) = 4.5
    c: Equal(g3,g1)
    c: Equal(g4,g5)
    c: Radius(g5) = 1
    c: Tangent(g6,g4) = 1.5708
    c: Tangent(g6,g5) = 1.5708
    c: Tangent(g4,g1) = -1.5708
    c: DistanceY(g2,g5) = 2.2
    c: DistanceX(g1,g2) = 7
    c: DistanceX(g7,g8) = 55
    c: Symmetric(g7,g8,g-2)
    c: Equal(g7,g8)
    c: Radius(g7) = 1.25
    c: DistanceY(g0,g7) = 7.4
FEATURE [PartDesign::Pocket] Pocket010  label="PocketKey"
  BaseFeature = -> Pocket005
  ClaimChildren = false
  Fit = 0
  FitJoin = 0
  InnerFit = 0
  InnerFitJoin = 0
  InnerTaperAngle = 0
  InnerTaperAngleRev = 0
  Length = 0
  Length2 = 100
  Midplane = true
  NewSolid = false
  Profile = -> Sketch037
  Suppress = false
  Type = 3
  UpToFace = -> Pocket005 [Face26]
FEATURE [PartDesign::SubtractiveLoft] SubtractiveLoft
  BaseFeature = -> Pocket010
  ClaimChildren = false
  Closed = false
  Fit = 0
  FitJoin = 0
  InnerFit = 0
  InnerFitJoin = 0
  NewSolid = false
  Profile = -> Sketch022
  Ruled = true
  Sections = -> [Sketch025,Sketch023]
  Suppress = false
FEATURE [PartDesign::Revolution] Revolution  label="RevolutionButton"
  Angle = 360
  Axis = (-1e-16,0.309017,0.951057)
  Base = (-4.6e-15,10,30.6)
  BaseFeature = -> SubtractiveLoft
  ClaimChildren = false
  Fit = 0
  FitJoin = 0
  InnerFit = 0
  InnerFitJoin = 0
  NewSolid = false
  Profile = -> Sketch021
  ReferenceAxis = -> Sketch021 [V_Axis]
  Reversed = true
  Suppress = false
FEATURE [PartDesign::Pocket] Pocket007  label="PocketButton"
  BaseFeature = -> Revolution
  ClaimChildren = false
  Fit = 0
  FitJoin = 0
  InnerFit = 0
  InnerFitJoin = 0
  InnerTaperAngle = 0
  InnerTaperAngleRev = 0
  Length = 14
  Length2 = 100
  NewSolid = false
  Profile = -> Sketch008
  Reversed = true
  Suppress = false
  Type = 0
FEATURE [PartDesign::Groove] Groove  label="GrooveButton"
  Angle = 360
  Axis = (-1e-16,0.309017,0.951057)
  Base = (-4.1e-15,10,28.6)
  BaseFeature = -> Pocket007
  ClaimChildren = false
  Fit = 0
  FitJoin = 0
  InnerFit = 0
  InnerFitJoin = 0
  NewSolid = false
  Profile = -> Sketch027
  ReferenceAxis = -> Sketch027 [V_Axis]
  Suppress = false
FEATURE [PartDesign::Pocket] Pocket004  label="PocketFrontScrews"
  BaseFeature = -> Groove
  ClaimChildren = false
  Fit = 0
  FitJoin = 0
  InnerFit = 0
  InnerFitJoin = 0
  InnerTaperAngle = 0
  InnerTaperAngleRev = 0
  Length = 5
  Length2 = 100
  NewSolid = false
  Profile = -> Sketch026
  Suppress = false
  Type = 0
FEATURE [PartDesign::Pocket] Pocket003  label="PocketFace"
  BaseFeature = -> Pocket004
  ClaimChildren = false
  Fit = 0
  FitJoin = 0
  InnerFit = 0
  InnerFitJoin = 0
  InnerTaperAngle = 0
  InnerTaperAngleRev = 0
  Length = 6
  Length2 = 100
  NewSolid = false
  Profile = -> Sketch024
  Reversed = true
  Suppress = false
  Type = 0
  expr: Length = <<param>>.face_thickness * 2
FEATURE [PartDesign::Fillet] Fillet005
  Base = -> Pocket003 [Edge122,Edge198]
  BaseFeature = -> Pocket003
  NewSolid = false
  Radius = 10
  SupportTransform = false
  Suppress = false
  expr: Radius = <<param>>.radius_big
FEATURE [PartDesign::Fillet] Fillet006
  Base = -> Fillet005 [Edge5]
  BaseFeature = -> Fillet005
  NewSolid = false
  Radius = 2
  SupportTransform = false
  Suppress = false
FEATURE [PartDesign::Fillet] Fillet007
  Base = -> Fillet006 [Edge7]
  BaseFeature = -> Fillet006
  NewSolid = false
  Radius = 2
  SupportTransform = false
  Suppress = false
FEATURE [PartDesign::Fillet] Fillet008
  Base = -> Fillet007 [Edge95]
  BaseFeature = -> Fillet007
  NewSolid = false
  Radius = 10
  SupportTransform = false
  Suppress = false
FEATURE [PartDesign::Body] Body004  label="BodyCase"
  AutoGroupSolids = false
  BaseFeature = -> Slice_child0
  ExportMode = 0
  Group = -> [BaseFeature001,Sketch008,Sketch029,Sketch018,Sketch019,Sketch021,Sketch022,Sketch023,Sketch024,Sketch025,Sketch026,Sketch027,Sketch028,Sketch,Pocket001,Pad,Pocket002,Pocket006,Pocket005,Pocket010,SubtractiveLoft,Revolution,Pocket007,Groove,Pocket004,Pocket003,Fillet005,Fillet006,Fillet007,Fillet008,Sketch037]
  Origin = -> Origin005
  Tip = -> Fillet008
  _ExportChildren = -> [BaseFeature001,Pocket001,Pad,Pocket002,Pocket006,Pocket005,Pocket010,SubtractiveLoft,Revolution,Pocket007,Groove,Pocket004,Pocket003,Fillet005,Fillet006,Fillet007,Fillet008]
  _GroupVersion = 1
FEATURE [Mesh::Feature] Mesh  label="BodyBack (Meshed)"
FEATURE [Mesh::Feature] Mesh004  label="BodyCase (Meshed)"
FEATURE [App::DocumentObjectGroup] Group  label="Mesh"
  ExportMode = 1
  Group = -> [Mesh002,Mesh003,Mesh,Mesh004]
  _GroupVersion = 1
FEATURE [App::Part] Part
  ExportMode = 1
  Group = -> [Extrude,Plane002,Common,Sketch012,Loft,Slice_child1,Slice_child0,Slice,GrExplode_Slice,Sketch030,Sketch031,Group001,Spreadsheet,Body,Body004,Body005,Body006,Mesh002,Group,Mesh003,Mesh,Mesh004]
  Origin = -> Origin006
  _ExportChildren = -> [Group001,Spreadsheet,Body,Body004,Body005,Body006,Group]
  _GroupVersion = 1
